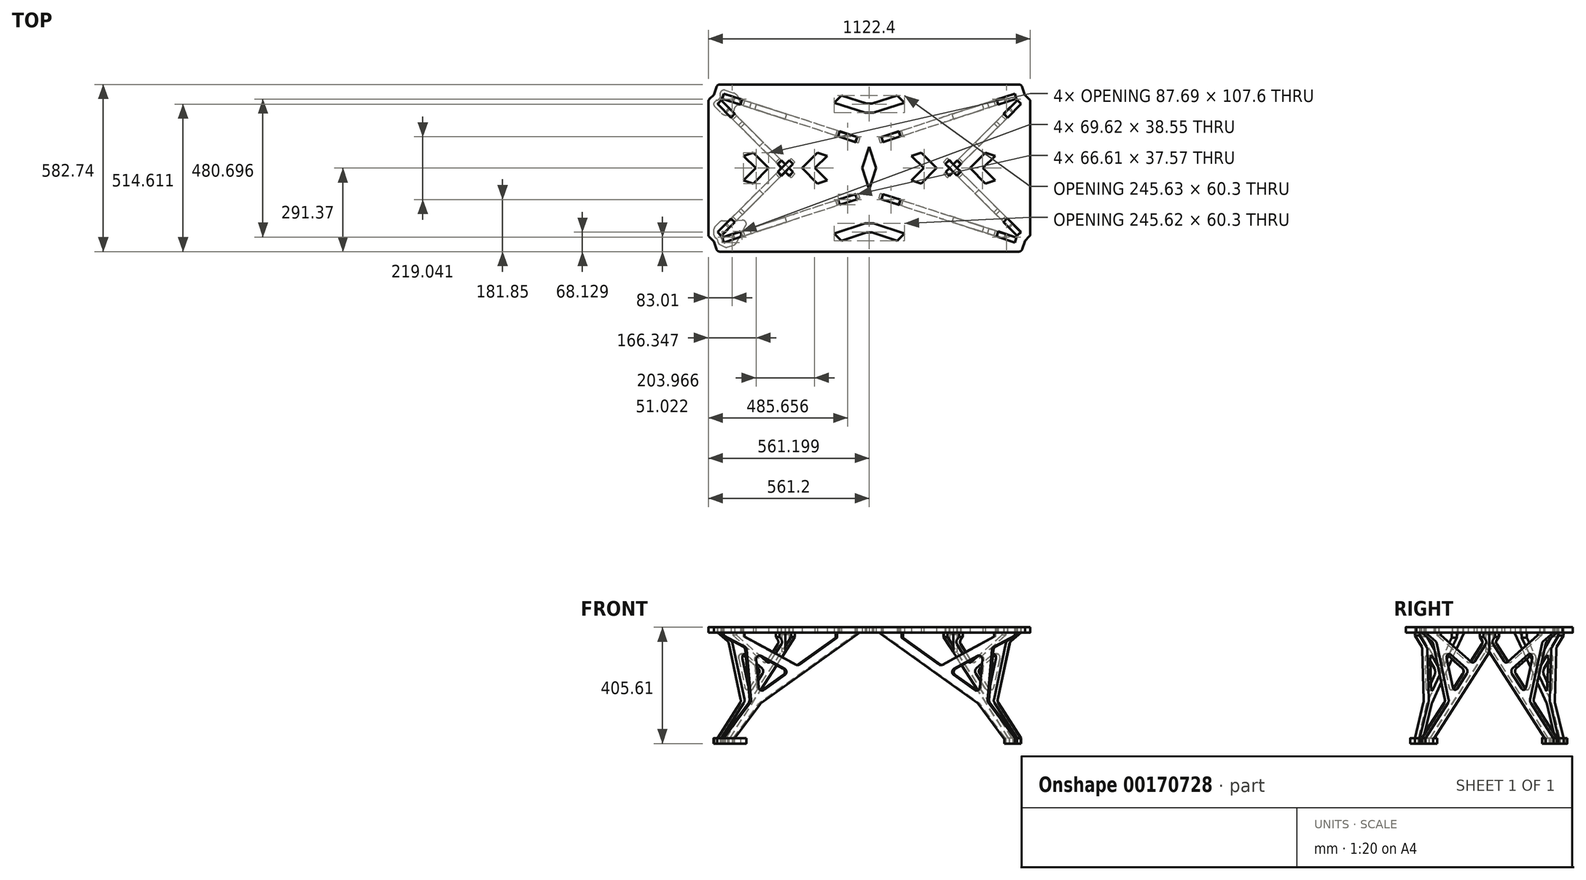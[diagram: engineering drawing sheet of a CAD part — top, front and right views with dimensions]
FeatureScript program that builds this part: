
annotation { "Feature Type Name" : "Feature", "Feature Type Description" : "" }
export const myFeature = defineFeature(function(context is Context, id is Id, definition is map)
    precondition{}
    {
        {
            var Q0;
            Q0=qCreatedBy(makeId("Top.planeOp"),FACE);
            var sketch = newSketch(context, id + "F0", { "sketchPlane" : qUnion([Q0])});
            skLineSegment(sketch, "E0.bottom", {"start": v(0, 0) * mm, "end": v(1117.6, 0) * mm});
            skLineSegment(sketch, "E0.top", {"start": v(0, 558.8) * mm, "end": v(1117.6, 558.8) * mm});
            skLineSegment(sketch, "E0.left", {"start": v(0, 0) * mm, "end": v(0, 558.8) * mm});
            skLineSegment(sketch, "E0.right", {"start": v(1117.6, 0) * mm, "end": v(1117.6, 558.8) * mm});
            skPoint(sketch, "E1", {"position": v(0, 279.4) * mm});
            skPoint(sketch, "E2", {"position": v(558.8, 558.8) * mm});
            skLineSegment(sketch, "E3", {"start": v(0, 279.4) * mm, "end": v(1117.6, 279.4) * mm, "construction": true});
            skLineSegment(sketch, "E4", {"start": v(558.8, 558.8) * mm, "end": v(558.8, 0) * mm, "construction": true});
            skLineSegment(sketch, "E5", {"start": v(0, 0) * mm, "end": v(42.87, 42.87) * mm, "construction": true});
            skLineSegment(sketch, "E6", {"start": v(0, 558.8) * mm, "end": v(33.89, 524.91) * mm, "construction": true});
            skLineSegment(sketch, "E7", {"start": v(1117.6, 558.8) * mm, "end": v(838.2, 279.4) * mm});
            skLineSegment(sketch, "E8", {"start": v(1117.6, 0) * mm, "end": v(838.2, 279.4) * mm});
            skLineSegment(sketch, "E9", {"start": v(279.4, 279.4) * mm, "end": v(299.6, 299.6) * mm});
            skLineSegment(sketch, "E10", {"start": v(279.4, 279.4) * mm, "end": v(299.6, 259.2) * mm});
            skLineSegment(sketch, "E11.0", {"start": v(19.05, 539.75) * mm, "end": v(1098.55, 539.75) * mm, "construction": true});
            skLineSegment(sketch, "E11.1", {"start": v(19.05, 19.05) * mm, "end": v(19.05, 32.52) * mm, "construction": true});
            skLineSegment(sketch, "E11.2", {"start": v(19.05, 19.05) * mm, "end": v(1098.55, 19.05) * mm, "construction": true});
            skLineSegment(sketch, "E11.3", {"start": v(1098.55, 19.05) * mm, "end": v(1098.55, 539.75) * mm, "construction": true});
            skLineSegment(sketch, "E12.trimOffspring", {"start": v(36.13, 49.6) * mm, "end": v(292.87, 306.34) * mm, "construction": true});
            skLineSegment(sketch, "E13", {"start": v(19.05, 539.75) * mm, "end": v(36.83, 533.97) * mm});
            skLineSegment(sketch, "E14", {"start": v(1098.55, 539.75) * mm, "end": v(558.8, 364.37) * mm});
            skLineSegment(sketch, "E15", {"start": v(1098.55, 19.05) * mm, "end": v(558.8, 194.43) * mm});
            skLineSegment(sketch, "E16", {"start": v(19.05, 19.05) * mm, "end": v(558.8, 194.43) * mm, "construction": true});
            skCircle(sketch, "E17", {"center": v(558.8, 279.4) * mm, "radius": 203.2 * mm});
            skPoint(sketch, "E18", {"position": v(330.81, 120.35) * mm});
            skPoint(sketch, "E19", {"position": v(442.7, 156.7) * mm});
            skPoint(sketch, "E20", {"position": v(406.46, 144.93) * mm});
            skPoint(sketch, "E21", {"position": v(406.46, 413.87) * mm});
            skPoint(sketch, "E22", {"position": v(370.23, 425.65) * mm});
            skPoint(sketch, "E23", {"position": v(711.14, 413.87) * mm});
            skPoint(sketch, "E24", {"position": v(747.37, 425.65) * mm});
            skPoint(sketch, "E25", {"position": v(674.9, 402.1) * mm});
            skPoint(sketch, "E26", {"position": v(711.14, 144.93) * mm});
            skPoint(sketch, "E27", {"position": v(674.9, 156.7) * mm});
            skPoint(sketch, "E28", {"position": v(747.37, 133.15) * mm});
            skLineSegment(sketch, "E29.bottom", {"start": v(-182.02, 259.46) * mm, "end": v(-105.82, 259.46) * mm});
            skLineSegment(sketch, "E29.top", {"start": v(-182.02, 278.51) * mm, "end": v(-105.82, 278.51) * mm});
            skLineSegment(sketch, "E29.left", {"start": v(-182.02, 259.46) * mm, "end": v(-182.02, 278.51) * mm});
            skLineSegment(sketch, "E29.right", {"start": v(-105.82, 259.46) * mm, "end": v(-105.82, 278.51) * mm});
            skLineSegment(sketch, "E30.bottom", {"start": v(-184.27, 473.53) * mm, "end": v(-82.67, 473.53) * mm});
            skLineSegment(sketch, "E30.top", {"start": v(-184.27, 492.58) * mm, "end": v(-82.67, 492.58) * mm});
            skLineSegment(sketch, "E30.left", {"start": v(-184.27, 473.53) * mm, "end": v(-184.27, 492.58) * mm});
            skLineSegment(sketch, "E30.right", {"start": v(-82.67, 473.53) * mm, "end": v(-82.67, 492.58) * mm});
            skPoint(sketch, "E31", {"position": v(-133.34, 483.2) * mm});
            skPoint(sketch, "E32", {"position": v(-133.34, 534) * mm});
            skLineSegment(sketch, "E33", {"start": v(-133.34, 534) * mm, "end": v(-123.82, 534) * mm});
            skLineSegment(sketch, "E34", {"start": v(-133.34, 534) * mm, "end": v(-142.87, 534) * mm});
            skLineSegment(sketch, "E35", {"start": v(-142.87, 534) * mm, "end": v(-144.35, 432.4) * mm});
            skLineSegment(sketch, "E36", {"start": v(-144.35, 432.4) * mm, "end": v(-125.29, 432.13) * mm});
            skLineSegment(sketch, "E37", {"start": v(-125.29, 432.13) * mm, "end": v(-123.82, 534) * mm});
            skPoint(sketch, "E38", {"position": v(-143.92, 268.99) * mm});
            skLineSegment(sketch, "E39", {"start": v(-153.47, 230.9) * mm, "end": v(-134.4, 230.9) * mm});
            skLineSegment(sketch, "E40", {"start": v(-134.4, 230.9) * mm, "end": v(-134.4, 307.1) * mm});
            skLineSegment(sketch, "E41", {"start": v(-134.4, 307.1) * mm, "end": v(-153.47, 307.1) * mm});
            skLineSegment(sketch, "E42", {"start": v(-153.47, 307.1) * mm, "end": v(-153.47, 230.9) * mm});
            skLineSegment(sketch, "E43.0", {"start": v(51.85, 19.7) * mm, "end": v(88.1, 31.47) * mm});
            skLineSegment(sketch, "E44.0", {"start": v(19.05, 29.07) * mm, "end": v(64.77, 43.92) * mm, "construction": true});
            skPoint(sketch, "E45", {"position": v(33.89, 33.89) * mm});
            skPoint(sketch, "E46", {"position": v(42.87, 42.87) * mm});
            skPoint(sketch, "E47", {"position": v(45.96, 37.81) * mm});
            skLineSegment(sketch, "E48", {"start": v(45.96, 37.81) * mm, "end": v(52.06, 19.05) * mm});
            skLineSegment(sketch, "E49", {"start": v(42.87, 42.87) * mm, "end": v(29.4, 56.33) * mm});
            skLineSegment(sketch, "E50.trimOffspring", {"start": v(19.05, 32.52) * mm, "end": v(19.05, 539.75) * mm, "construction": true});
            skLineSegment(sketch, "E51", {"start": v(29.4, 56.33) * mm, "end": v(56.34, 83.27) * mm});
            skLineSegment(sketch, "E52", {"start": v(69.8, 69.8) * mm, "end": v(42.87, 42.87) * mm});
            skLineSegment(sketch, "E53", {"start": v(45.96, 37.81) * mm, "end": v(82.2, 49.59) * mm});
            skPoint(sketch, "E54.visualSharp", {"position": v(19.05, 54.96) * mm});
            skPoint(sketch, "E55.orphan", {"position": v(53.81, 13.65) * mm});
            skPoint(sketch, "E56.visualSharp", {"position": v(69.8, 69.8) * mm});
            skPoint(sketch, "E57.visualSharp", {"position": v(82.2, 49.59) * mm});
            skLineSegment(sketch, "E58", {"start": v(245.72, 245.72) * mm, "end": v(232.25, 259.2) * mm});
            skLineSegment(sketch, "E59", {"start": v(299.6, 299.6) * mm, "end": v(286.14, 313.08) * mm});
            skLineSegment(sketch, "E60", {"start": v(265.93, 292.87) * mm, "end": v(286.14, 313.08) * mm});
            skLineSegment(sketch, "E61", {"start": v(299.6, 259.2) * mm, "end": v(286.14, 245.72) * mm});
            skPoint(sketch, "E62", {"position": v(245.72, 313.08) * mm});
            skLineSegment(sketch, "E63", {"start": v(245.72, 313.08) * mm, "end": v(232.25, 299.6) * mm});
            skPoint(sketch, "E64.orphan", {"position": v(272.66, 286.14) * mm});
            skLineSegment(sketch, "E65", {"start": v(36.13, 49.6) * mm, "end": v(90, 103.48) * mm});
            skPoint(sketch, "E66", {"position": v(403.28, 143.9) * mm});
            skLineSegment(sketch, "E67.0", {"start": v(19.05, 529.73) * mm, "end": v(33.89, 524.91) * mm, "construction": true});
            skLineSegment(sketch, "E68.0", {"start": v(51.85, 539.1) * mm, "end": v(88.09, 527.33) * mm, "construction": true});
            skPoint(sketch, "E69", {"position": v(33.89, 524.91) * mm});
            skPoint(sketch, "E70", {"position": v(45.96, 520.99) * mm});
            skPoint(sketch, "E71", {"position": v(42.87, 515.93) * mm});
            skLineSegment(sketch, "E72", {"start": v(42.87, 515.93) * mm, "end": v(29.4, 502.46) * mm, "construction": true});
            skLineSegment(sketch, "E73", {"start": v(45.96, 520.99) * mm, "end": v(51.85, 539.1) * mm});
            skLineSegment(sketch, "E74", {"start": v(51.85, 539.1) * mm, "end": v(82.05, 529.3) * mm});
            skLineSegment(sketch, "E75", {"start": v(76.16, 511.18) * mm, "end": v(45.96, 520.99) * mm});
            skLineSegment(sketch, "E76", {"start": v(33.89, 524.91) * mm, "end": v(24.9, 515.93) * mm});
            skLineSegment(sketch, "E77", {"start": v(33.89, 524.91) * mm, "end": v(37.81, 537) * mm});
            skLineSegment(sketch, "E78.0", {"start": v(43.7, 555.11) * mm, "end": v(55.78, 551.19) * mm});
            skLineSegment(sketch, "E79.0", {"start": v(11.43, 502.46) * mm, "end": v(20.42, 493.48) * mm});
            skPoint(sketch, "E80", {"position": v(122.52, 529.5) * mm});
            skLineSegment(sketch, "E81.trimOffspring", {"start": v(19.05, 526.28) * mm, "end": v(27.15, 518.18) * mm, "construction": true});
            skLineSegment(sketch, "E82.trimOffspring", {"start": v(19.05, 512.8) * mm, "end": v(29.4, 502.46) * mm, "construction": true});
            skPoint(sketch, "E83", {"position": v(20.42, 493.48) * mm});
            skPoint(sketch, "E84", {"position": v(20.42, 511.44) * mm});
            skArc(sketch, "E85.trimOffspring", {"start": v(20.42, 511.44) * mm, "mid": v(16.32, 502.46) * mm, "end": v(20.42, 493.48) * mm});
            skPoint(sketch, "E86", {"position": v(24.9, 515.93) * mm});
            skPoint(sketch, "E87", {"position": v(37.81, 537) * mm});
            skLineSegment(sketch, "E88.trimOffspring", {"start": v(45.96, 520.99) * mm, "end": v(82.2, 509.22) * mm, "construction": true});
            skLineSegment(sketch, "E89.trimOffspring", {"start": v(36.13, 509.2) * mm, "end": v(58.58, 486.75) * mm, "construction": true});
            skLineSegment(sketch, "E90.trimOffspring", {"start": v(48.9, 530.05) * mm, "end": v(79.1, 520.24) * mm});
            skArc(sketch, "E91", {"start": v(27.07, 515.93) * mm, "mid": v(37.83, 522.5) * mm, "end": v(38.8, 535.07) * mm});
            skPoint(sketch, "E91.third.point", {"position": v(12.19, 529.33) * mm});
            skPoint(sketch, "E92", {"position": v(39.77, 543.03) * mm});
            skPoint(sketch, "E93", {"position": v(55.78, 551.19) * mm});
            skLineSegment(sketch, "E94.trimOffspring", {"start": v(39.77, 543.03) * mm, "end": v(43.7, 555.11) * mm});
            skArc(sketch, "E95.trimOffspring", {"start": v(55.78, 551.19) * mm, "mid": v(46.26, 550.07) * mm, "end": v(39.77, 543.03) * mm});
            skLineSegment(sketch, "E96", {"start": v(33.89, 524.91) * mm, "end": v(176.88, 437.29) * mm, "construction": true});
            skPoint(sketch, "E97", {"position": v(51.85, 462.05) * mm});
            skPoint(sketch, "E98", {"position": v(98.05, 537.45) * mm});
            skLineSegment(sketch, "E99", {"start": v(64.47, 463.46) * mm, "end": v(82.68, 465.5) * mm});
            skLineSegment(sketch, "E100", {"start": v(108.97, 508.42) * mm, "end": v(102.52, 525.56) * mm});
            skPoint(sketch, "E101", {"position": v(64.47, 463.46) * mm});
            skPoint(sketch, "E102", {"position": v(102.52, 525.56) * mm});
            skArc(sketch, "E103", {"start": v(42.87, 471.03) * mm, "mid": v(54.55, 464.49) * mm, "end": v(67.94, 463.92) * mm});
            skArc(sketch, "E104", {"start": v(103.55, 522.31) * mm, "mid": v(97.05, 534.27) * mm, "end": v(85.53, 541.52) * mm});
            skArc(sketch, "E105", {"start": v(104, 499.9) * mm, "mid": v(89.94, 490.56) * mm, "end": v(88, 473.8) * mm});
            skPoint(sketch, "E105.first.point", {"position": v(92.23, 466.57) * mm});
            skPoint(sketch, "E105.second.point", {"position": v(112.36, 499.42) * mm});
            skLineSegment(sketch, "E106.trimOffspring", {"start": v(93.52, 465.28) * mm, "end": v(279.4, 279.4) * mm, "construction": true});
            skLineSegment(sketch, "E107.trimOffspring", {"start": v(114.1, 498.85) * mm, "end": v(552.91, 356.27) * mm, "construction": true});
            skArc(sketch, "E108.filletArc", {"start": v(82.68, 465.5) * mm, "mid": v(87.31, 468.38) * mm, "end": v(88, 473.8) * mm});
            skArc(sketch, "E109.filletArc", {"start": v(104, 499.9) * mm, "mid": v(108.5, 502.97) * mm, "end": v(108.97, 508.42) * mm});
            skLineSegment(sketch, "E110", {"start": v(38.62, 539.48) * mm, "end": v(39.77, 543.03) * mm});
            skLineSegment(sketch, "E111.trimOffspring", {"start": v(20.42, 511.44) * mm, "end": v(11.43, 502.46) * mm});
            skLineSegment(sketch, "E112", {"start": v(20.42, 511.44) * mm, "end": v(23.06, 514.09) * mm});
            skArc(sketch, "E113.filletArc", {"start": v(27.07, 515.93) * mm, "mid": v(24.9, 515.37) * mm, "end": v(23.06, 514.09) * mm});
            skArc(sketch, "E114.filletArc", {"start": v(38.62, 539.48) * mm, "mid": v(38.31, 537.26) * mm, "end": v(38.8, 535.07) * mm});
            skLineSegment(sketch, "E115.trimOffspring", {"start": v(42.87, 471.03) * mm, "end": v(65.33, 448.56) * mm});
            skLineSegment(sketch, "E116", {"start": v(42.87, 471.03) * mm, "end": v(20.42, 493.48) * mm});
            skLineSegment(sketch, "E117.trimOffspring", {"start": v(85.53, 541.52) * mm, "end": v(122.52, 529.5) * mm});
            skLineSegment(sketch, "E118", {"start": v(85.53, 541.52) * mm, "end": v(55.78, 551.19) * mm});
            skLineSegment(sketch, "E119.trimOffspring", {"start": v(108.06, 510.83) * mm, "end": v(558.8, 364.37) * mm});
            skLineSegment(sketch, "E120.trimOffspring", {"start": v(80.11, 465.22) * mm, "end": v(292.87, 252.46) * mm, "construction": true});
            skLineSegment(sketch, "E121.trimOffspring", {"start": v(51.86, 480) * mm, "end": v(286.14, 245.72) * mm, "construction": true});
            skLineSegment(sketch, "E122", {"start": v(29.4, 502.46) * mm, "end": v(51.85, 480.02) * mm, "construction": true});
            skLineSegment(sketch, "E123.0", {"start": v(42.87, 516.04) * mm, "end": v(29.29, 502.46) * mm});
            skLineSegment(sketch, "E124.0", {"start": v(29.29, 502.46) * mm, "end": v(56.32, 475.44) * mm});
            skLineSegment(sketch, "E125.trimOffspring", {"start": v(88.2, 470.6) * mm, "end": v(92.23, 466.57) * mm, "construction": true});
            skLineSegment(sketch, "E126", {"start": v(42.87, 515.93) * mm, "end": v(65.32, 493.48) * mm, "construction": true});
            skLineSegment(sketch, "E127", {"start": v(69.8, 489.03) * mm, "end": v(56.32, 475.54) * mm, "construction": true});
            skLineSegment(sketch, "E128", {"start": v(56.32, 475.54) * mm, "end": v(51.86, 480) * mm});
            skLineSegment(sketch, "E129.0", {"start": v(69.9, 489.01) * mm, "end": v(56.32, 475.44) * mm});
            skLineSegment(sketch, "E130", {"start": v(76.16, 511.18) * mm, "end": v(82.2, 509.22) * mm});
            skLineSegment(sketch, "E131", {"start": v(82.2, 509.22) * mm, "end": v(88.09, 527.33) * mm, "construction": true});
            skLineSegment(sketch, "E132", {"start": v(88.09, 527.33) * mm, "end": v(82.05, 529.3) * mm, "construction": true});
            skLineSegment(sketch, "E133.0", {"start": v(82.25, 509.12) * mm, "end": v(88.18, 527.38) * mm});
            skLineSegment(sketch, "E134", {"start": v(82.27, 509.2) * mm, "end": v(82.2, 509.22) * mm});
            skLineSegment(sketch, "E135", {"start": v(558.8, 374.39) * mm, "end": v(552.91, 356.27) * mm, "construction": true});
            skLineSegment(sketch, "E136", {"start": v(413.61, 421.56) * mm, "end": v(407.73, 403.45) * mm, "construction": true});
            skPoint(sketch, "E137", {"position": v(480.32, 379.86) * mm});
            skLineSegment(sketch, "E138", {"start": v(480.32, 379.86) * mm, "end": v(450.12, 389.67) * mm});
            skLineSegment(sketch, "E139", {"start": v(450.12, 389.67) * mm, "end": v(456, 407.79) * mm});
            skLineSegment(sketch, "E140", {"start": v(456, 407.79) * mm, "end": v(516.4, 388.17) * mm});
            skLineSegment(sketch, "E141", {"start": v(516.4, 388.17) * mm, "end": v(510.5, 370.05) * mm});
            skLineSegment(sketch, "E142", {"start": v(510.5, 370.05) * mm, "end": v(480.32, 379.86) * mm});
            skLineSegment(sketch, "E143", {"start": v(19.05, 19.05) * mm, "end": v(48.9, 28.75) * mm});
            skPoint(sketch, "E144", {"position": v(1068.7, 28.75) * mm});
            skLineSegment(sketch, "E145", {"start": v(1065.74, 19.68) * mm, "end": v(1071.63, 37.8) * mm});
            skLineSegment(sketch, "E146", {"start": v(1071.63, 37.8) * mm, "end": v(1035.4, 49.58) * mm});
            skLineSegment(sketch, "E147", {"start": v(1035.4, 49.58) * mm, "end": v(1029.51, 31.45) * mm});
            skPoint(sketch, "E148", {"position": v(1073.92, 43.68) * mm});
            skLineSegment(sketch, "E149", {"start": v(1073.92, 43.68) * mm, "end": v(1087.39, 57.15) * mm});
            skLineSegment(sketch, "E150", {"start": v(1087.39, 57.15) * mm, "end": v(1060.45, 84.1) * mm});
            skLineSegment(sketch, "E151", {"start": v(1060.45, 84.1) * mm, "end": v(1046.98, 70.62) * mm});
            skLineSegment(sketch, "E152", {"start": v(1046.98, 70.62) * mm, "end": v(1073.92, 43.68) * mm});
            skPoint(sketch, "E153", {"position": v(1053.71, 77.36) * mm});
            skLineSegment(sketch, "E154", {"start": v(1053.71, 77.36) * mm, "end": v(1080.65, 50.42) * mm, "construction": true});
            skPoint(sketch, "E155", {"position": v(1068.7, 530.05) * mm});
            skLineSegment(sketch, "E156", {"start": v(1071.63, 521) * mm, "end": v(1065.75, 539.1) * mm});
            skLineSegment(sketch, "E157", {"start": v(1065.75, 539.1) * mm, "end": v(1029.52, 527.33) * mm});
            skLineSegment(sketch, "E158", {"start": v(1029.52, 527.33) * mm, "end": v(1035.4, 509.22) * mm});
            skLineSegment(sketch, "E159", {"start": v(1035.4, 509.22) * mm, "end": v(1071.63, 521) * mm});
            skPoint(sketch, "E160", {"position": v(1074.74, 515.94) * mm});
            skLineSegment(sketch, "E161", {"start": v(1074.74, 515.94) * mm, "end": v(1088.2, 502.47) * mm});
            skLineSegment(sketch, "E162", {"start": v(1088.2, 502.47) * mm, "end": v(1061.26, 475.53) * mm});
            skLineSegment(sketch, "E163", {"start": v(1061.26, 475.53) * mm, "end": v(1047.8, 489) * mm});
            skLineSegment(sketch, "E164", {"start": v(1047.8, 489) * mm, "end": v(1074.74, 515.94) * mm});
            skPoint(sketch, "E165", {"position": v(1054.53, 482.26) * mm});
            skLineSegment(sketch, "E166", {"start": v(1054.53, 482.26) * mm, "end": v(1081.47, 509.2) * mm, "construction": true});
            skLineSegment(sketch, "E167", {"start": v(82.2, 49.59) * mm, "end": v(88.1, 31.47) * mm});
            skLineSegment(sketch, "E168.trimOffspring", {"start": v(88.1, 31.47) * mm, "end": v(561.74, 185.37) * mm, "construction": true});
            skLineSegment(sketch, "E169.trimOffspring", {"start": v(82.2, 49.59) * mm, "end": v(555.86, 203.48) * mm, "construction": true});
            skLineSegment(sketch, "E170.trimOffspring", {"start": v(69.8, 69.8) * mm, "end": v(279.4, 279.4) * mm, "construction": true});
            skLineSegment(sketch, "E171", {"start": v(69.8, 69.8) * mm, "end": v(56.34, 83.28) * mm});
            skLineSegment(sketch, "E172", {"start": v(1065.74, 19.68) * mm, "end": v(1029.51, 31.45) * mm});
            skPoint(sketch, "E173.end.orphan", {"position": v(1083.72, 524.92) * mm});
            skLineSegment(sketch, "E174.0", {"start": v(42.87, 516.04) * mm, "end": v(69.9, 489.01) * mm});
            skLineSegment(sketch, "E175.trimOffspring", {"start": v(106.94, 501.18) * mm, "end": v(112.36, 499.42) * mm, "construction": true});
            skLineSegment(sketch, "E176.trimOffspring", {"start": v(103.55, 522.31) * mm, "end": v(561.74, 373.43) * mm, "construction": true});
            skLineSegment(sketch, "E177.0", {"start": v(51.8, 539.2) * mm, "end": v(88.18, 527.38) * mm});
            skLineSegment(sketch, "E177.1", {"start": v(45.87, 520.94) * mm, "end": v(51.8, 539.2) * mm});
            skLineSegment(sketch, "E177.2", {"start": v(45.87, 520.94) * mm, "end": v(82.25, 509.12) * mm});
            skSolve(sketch);
        }
        {
            var Q0;
            Q0=sQuery(id+"F0.wireOp",EDGE,"E16");
            cPlane(context, id + "F1", {"entities" : qUnion([Q0]), "cplaneType" : CPlaneType.LINE_ANGLE, "offset" : 25.4 * mm, "angle" : 0 * degree, "width" : 152.4 * mm, "height" : 152.4 * mm});
        }
        {
            var Q0;
            Q0=qCreatedBy(id+"F1.planeOp",FACE);
            var sketch = newSketch(context, id + "F2", { "sketchPlane" : qUnion([Q0])});
            skLineSegment(sketch, "E178.MirrorCS", {"start": v(-55.4, 387.35) * mm, "end": v(-55.4, 405.61) * mm});
            skLineSegment(sketch, "E179.MirrorCS", {"start": v(-55.4, 19.05) * mm, "end": v(-55.4, 0) * mm});
            skLineSegment(sketch, "E180.MirrorCS", {"start": v(-55.4, 0) * mm, "end": v(-93.5, 0) * mm});
            skLineSegment(sketch, "E181.MirrorCS", {"start": v(-131.6, 387.35) * mm, "end": v(-122.07, 387.35) * mm});
            skLineSegment(sketch, "E182.MirrorCS", {"start": v(-122.07, 405.61) * mm, "end": v(-122.07, 387.35) * mm});
            skLineSegment(sketch, "E183.MirrorCS", {"start": v(-93.5, 0) * mm, "end": v(-93.5, 19.05) * mm});
            skLineSegment(sketch, "E184.MirrorCS", {"start": v(-131.6, 387.35) * mm, "end": v(-131.6, 373.26) * mm});
            skPoint(sketch, "E185.MirrorP", {"position": v(-87.16, 0) * mm});
            skLineSegment(sketch, "E186.MirrorCS", {"start": v(-199.46, 139.13) * mm, "end": v(-199.94, 139.68) * mm});
            skLineSegment(sketch, "E187.MirrorCS", {"start": v(-131.6, 373.26) * mm, "end": v(-319.77, 274.75) * mm});
            skPoint(sketch, "E188.MirrorP", {"position": v(-55.4, 19.05) * mm});
            skLineSegment(sketch, "E189.MirrorCS", {"start": v(-189.04, 192.2) * mm, "end": v(-187.9, 197.99) * mm});
            skLineSegment(sketch, "E190.MirrorCS", {"start": v(-199.46, 139.13) * mm, "end": v(-199.43, 139.3) * mm});
            skLineSegment(sketch, "E191.trimOffspring", {"start": v(-199.94, 139.68) * mm, "end": v(-199.43, 139.3) * mm});
            skLineSegment(sketch, "E192", {"start": v(-480.35, 387.35) * mm, "end": v(-470.81, 387.35) * mm});
            skLineSegment(sketch, "E193", {"start": v(-543.85, 387.35) * mm, "end": v(-553.36, 387.35) * mm});
            skLineSegment(sketch, "E194", {"start": v(-470.81, 387.35) * mm, "end": v(-470.81, 369.53) * mm});
            skLineSegment(sketch, "E195", {"start": v(-543.85, 387.35) * mm, "end": v(-543.85, 405.61) * mm});
            skLineSegment(sketch, "E196", {"start": v(-480.35, 387.35) * mm, "end": v(-480.35, 405.61) * mm});
            skLineSegment(sketch, "E197", {"start": v(-553.36, 387.35) * mm, "end": v(-192.29, 141.35) * mm});
            skLineSegment(sketch, "E198.trimOffspring", {"start": v(-470.81, 369.53) * mm, "end": v(-332.8, 275.5) * mm});
            skPoint(sketch, "E199", {"position": v(-320.5, 267.12) * mm});
            skLineSegment(sketch, "E200", {"start": v(-55.4, 19.05) * mm, "end": v(-152.69, 143.25) * mm});
            skLineSegment(sketch, "E201.0", {"start": v(-80.4, -0.53) * mm, "end": v(-80.8, 0) * mm});
            skLineSegment(sketch, "E202", {"start": v(-93.5, 19.05) * mm, "end": v(-95.73, 19.05) * mm});
            skLineSegment(sketch, "E203.trimOffspring", {"start": v(-95.73, 19.05) * mm, "end": v(-189.44, 138.69) * mm});
            skLineSegment(sketch, "E204.0", {"start": v(-55.4, 377.31) * mm, "end": v(-132.58, 336.91) * mm});
            skLineSegment(sketch, "E205.trimOffspring", {"start": v(-279.27, 239.03) * mm, "end": v(-202.97, 187.05) * mm});
            skLineSegment(sketch, "E206", {"start": v(-55.4, 377.31) * mm, "end": v(-55.4, 387.35) * mm});
            skLineSegment(sketch, "E207", {"start": v(-155.34, 152.24) * mm, "end": v(-139.33, 326.82) * mm});
            skLineSegment(sketch, "E208.0", {"start": v(-183.17, 196.38) * mm, "end": v(-174.32, 292.94) * mm});
            skLineSegment(sketch, "E209.trimOffspring", {"start": v(-192.86, 305.35) * mm, "end": v(-278, 260.77) * mm});
            skPoint(sketch, "E210.trimOffspring.end.orphan", {"position": v(-160.66, 158.22) * mm});
            skPoint(sketch, "E211.orphan", {"position": v(-334.34, 267.12) * mm});
            skPoint(sketch, "E212.visualSharp", {"position": v(-296.77, 250.95) * mm});
            skArc(sketch, "E212.filletArc", {"start": v(-278, 260.77) * mm, "mid": v(-284.8, 250.26) * mm, "end": v(-279.27, 239.03) * mm});
            skPoint(sketch, "E213.visualSharp", {"position": v(-172.2, 316.17) * mm});
            skArc(sketch, "E213.filletArc", {"start": v(-174.32, 292.94) * mm, "mid": v(-179.9, 304.65) * mm, "end": v(-192.86, 305.35) * mm});
            skPoint(sketch, "E214.visualSharp", {"position": v(-185.14, 174.9) * mm});
            skArc(sketch, "E214.filletArc", {"start": v(-202.97, 187.05) * mm, "mid": v(-190.4, 186.05) * mm, "end": v(-183.17, 196.38) * mm});
            skPoint(sketch, "E215.visualSharp", {"position": v(-190.66, 140.24) * mm});
            skArc(sketch, "E215.filletArc", {"start": v(-189.44, 138.69) * mm, "mid": v(-190.76, 140.13) * mm, "end": v(-192.29, 141.35) * mm});
            skPoint(sketch, "E216.visualSharp", {"position": v(-326.52, 271.22) * mm});
            skArc(sketch, "E216.filletArc", {"start": v(-332.8, 275.5) * mm, "mid": v(-326.4, 273.32) * mm, "end": v(-319.77, 274.75) * mm});
            skPoint(sketch, "E217.visualSharp", {"position": v(-138.7, 333.7) * mm});
            skArc(sketch, "E217.filletArc", {"start": v(-132.58, 336.91) * mm, "mid": v(-137.24, 332.72) * mm, "end": v(-139.33, 326.82) * mm});
            skPoint(sketch, "E218.visualSharp", {"position": v(-155.8, 147.22) * mm});
            skArc(sketch, "E218.filletArc", {"start": v(-155.34, 152.24) * mm, "mid": v(-154.87, 147.5) * mm, "end": v(-152.69, 143.25) * mm});
            skLineSegment(sketch, "E219", {"start": v(-480.35, 405.61) * mm, "end": v(-543.85, 405.61) * mm});
            skLineSegment(sketch, "E220", {"start": v(-122.07, 405.61) * mm, "end": v(-55.4, 405.61) * mm});
            skSolve(sketch);
        }
        {
            var Q0;
            Q0=makeQuery(id+"F2.imprint","IMPRINT",FACE,{"disambiguationData":[TD([[makeQuery(id+"F2.imprint","IMPRINT",EDGE,{"derivedFrom":sQuery(id+"F2.wireOp",EDGE,"E187.MirrorCS")}),1.0]])]});
            extrude(context, id + "F3", {"entities" : qUnion([Q0]), "endBound" : BoundingType.SYMMETRIC, "depth" : 18.26 * mm});
        }
        {
            var Q0;
            Q0=sQuery(id+"F0.wireOp",EDGE,"E12.trimOffspring");
            cPlane(context, id + "F4", {"entities" : qUnion([Q0]), "cplaneType" : CPlaneType.LINE_ANGLE, "offset" : 25.4 * mm, "angle" : 90 * degree, "width" : 152.4 * mm, "height" : 152.4 * mm});
        }
        {
            var Q0;
            Q0=qCreatedBy(id+"F4.planeOp",FACE);
            var sketch = newSketch(context, id + "F5", { "sketchPlane" : qUnion([Q0])});
            skLineSegment(sketch, "E221.MirrorCS", {"start": v(347.5, 387.35) * mm, "end": v(357.03, 387.35) * mm});
            skArc(sketch, "E222.MirrorCS", {"start": v(110.82, 356.2) * mm, "mid": v(114.2, 353.14) * mm, "end": v(116.29, 349.08) * mm});
            skArc(sketch, "E223.MirrorCS", {"start": v(174.96, 154.1) * mm, "mid": v(175.2, 147.64) * mm, "end": v(172.2, 141.9) * mm});
            skLineSegment(sketch, "E224.MirrorCS", {"start": v(347.5, 371.58) * mm, "end": v(356.35, 363.54) * mm});
            skLineSegment(sketch, "E225.MirrorCS", {"start": v(60.62, 19.05) * mm, "end": v(60.62, 0) * mm});
            skLineSegment(sketch, "E226.MirrorCS", {"start": v(423.7, 387.35) * mm, "end": v(414.18, 387.35) * mm});
            skLineSegment(sketch, "E227.MirrorCS", {"start": v(347.5, 371.58) * mm, "end": v(347.5, 387.35) * mm});
            skLineSegment(sketch, "E228.MirrorCS", {"start": v(60.62, 387.35) * mm, "end": v(60.62, 405.61) * mm});
            skArc(sketch, "E229.MirrorCS", {"start": v(303.4, 286.35) * mm, "mid": v(295.76, 282.3) * mm, "end": v(287.3, 284.1) * mm});
            skArc(sketch, "E230.MirrorCS", {"start": v(217.03, 191.26) * mm, "mid": v(204.83, 187.41) * mm, "end": v(195.47, 196.14) * mm});
            skLineSegment(sketch, "E231.MirrorCS", {"start": v(357.03, 387.35) * mm, "end": v(357.03, 405.61) * mm});
            skLineSegment(sketch, "E232.MirrorCS", {"start": v(414.18, 387.35) * mm, "end": v(414.18, 405.61) * mm});
            skArc(sketch, "E233.MirrorCS", {"start": v(356.35, 363.54) * mm, "mid": v(360.5, 354.75) * mm, "end": v(357.22, 345.6) * mm});
            skArc(sketch, "E234.MirrorCS", {"start": v(261.62, 262.66) * mm, "mid": v(267.5, 253.63) * mm, "end": v(264.33, 243.33) * mm});
            skLineSegment(sketch, "E235.MirrorCS", {"start": v(136.81, 387.35) * mm, "end": v(136.81, 377.45) * mm});
            skLineSegment(sketch, "E236.MirrorCS", {"start": v(136.81, 387.35) * mm, "end": v(127.29, 387.35) * mm});
            skLineSegment(sketch, "E237.MirrorCS", {"start": v(98.72, 0) * mm, "end": v(98.72, 19.05) * mm});
            skLineSegment(sketch, "E238.MirrorCS", {"start": v(103.51, 19.05) * mm, "end": v(98.72, 19.05) * mm});
            skLineSegment(sketch, "E239.MirrorCS", {"start": v(127.29, 405.61) * mm, "end": v(127.29, 387.35) * mm});
            skArc(sketch, "E240.MirrorCS", {"start": v(165.35, 296.24) * mm, "mid": v(169.78, 309.98) * mm, "end": v(184.2, 310.69) * mm});
            skPoint(sketch, "E241.MirrorP", {"position": v(274.58, 254.62) * mm});
            skPoint(sketch, "E242.MirrorP", {"position": v(177.04, 147.22) * mm});
            skPoint(sketch, "E243.MirrorP", {"position": v(365.75, 355) * mm});
            skPoint(sketch, "E244.MirrorP", {"position": v(114.9, 353.68) * mm});
            skPoint(sketch, "E245.MirrorP", {"position": v(92.38, 0) * mm});
            skPoint(sketch, "E246.MirrorP", {"position": v(60.62, 19.05) * mm});
            skLineSegment(sketch, "E247.MirrorCS", {"start": v(60.62, 19.05) * mm, "end": v(172.2, 141.9) * mm});
            skLineSegment(sketch, "E248.MirrorCS", {"start": v(116.29, 349.08) * mm, "end": v(174.96, 154.1) * mm});
            skLineSegment(sketch, "E249.MirrorCS", {"start": v(184.2, 310.69) * mm, "end": v(261.62, 262.66) * mm});
            skLineSegment(sketch, "E250.MirrorCS", {"start": v(103.51, 19.05) * mm, "end": v(376.24, 319.33) * mm});
            skPoint(sketch, "E251.MirrorP", {"position": v(296.29, 278.52) * mm});
            skPoint(sketch, "E252.MirrorP", {"position": v(155.67, 328.39) * mm});
            skLineSegment(sketch, "E253.MirrorCS", {"start": v(303.4, 286.35) * mm, "end": v(357.22, 345.6) * mm});
            skLineSegment(sketch, "E254.MirrorCS", {"start": v(60.62, 0) * mm, "end": v(98.72, 0) * mm});
            skLineSegment(sketch, "E255.MirrorCS", {"start": v(136.81, 377.45) * mm, "end": v(287.3, 284.1) * mm});
            skLineSegment(sketch, "E256.MirrorCS", {"start": v(165.35, 296.24) * mm, "end": v(195.47, 196.14) * mm});
            skLineSegment(sketch, "E257.MirrorCS", {"start": v(217.03, 191.26) * mm, "end": v(264.33, 243.33) * mm});
            skLineSegment(sketch, "E258.MirrorCS", {"start": v(60.62, 387.35) * mm, "end": v(110.82, 356.2) * mm});
            skPoint(sketch, "E259.MirrorP", {"position": v(201.94, 174.64) * mm});
            skLineSegment(sketch, "E260.MirrorCS", {"start": v(423.7, 371.58) * mm, "end": v(423.7, 387.35) * mm});
            skLineSegment(sketch, "E261.trimOffspring", {"start": v(394.96, 339.94) * mm, "end": v(423.7, 371.58) * mm});
            skLineSegment(sketch, "E262.0", {"start": v(376.24, 380.97) * mm, "end": v(376.24, 319.33) * mm});
            skLineSegment(sketch, "E263.0", {"start": v(394.96, 380.97) * mm, "end": v(394.96, 339.94) * mm});
            skLineSegment(sketch, "E264.trimOffspring", {"start": v(376.24, 380.97) * mm, "end": v(394.96, 380.97) * mm});
            skLineSegment(sketch, "E265", {"start": v(414.18, 405.61) * mm, "end": v(357.03, 405.61) * mm});
            skLineSegment(sketch, "E266.trimOffspring", {"start": v(127.29, 405.61) * mm, "end": v(60.62, 405.61) * mm});
            skSolve(sketch);
        }
        {
            var Q0;
            Q0 = qSketchRegion(id + "F5", true);
            extrude(context, id + "F6", {"entities" : qUnion([Q0]), "endBound" : BoundingType.SYMMETRIC, "depth" : 18.26 * mm});
        }
        {
            var Q0;
            Q0=sQuery(id+"F0.wireOp",EDGE,"E89.trimOffspring");
            cPlane(context, id + "F7", {"entities" : qUnion([Q0]), "cplaneType" : CPlaneType.LINE_ANGLE, "offset" : 25.4 * mm, "angle" : 90 * degree, "width" : 152.4 * mm, "height" : 152.4 * mm});
        }
        {
            var Q0;
            Q0=qCreatedBy(id+"F7.planeOp",FACE);
            var sketch = newSketch(context, id + "F8", { "sketchPlane" : qUnion([Q0])});
            skLineSegment(sketch, "E267.MirrorCS", {"start": v(-28.57, 387.35) * mm, "end": v(-19.05, 387.35) * mm});
            skLineSegment(sketch, "E268.MirrorCS", {"start": v(47.62, 387.35) * mm, "end": v(38.1, 387.35) * mm});
            skLineSegment(sketch, "E269.MirrorCS", {"start": v(258.31, 387.35) * mm, "end": v(267.84, 387.35) * mm});
            skLineSegment(sketch, "E270.MirrorCS", {"start": v(334.5, 387.35) * mm, "end": v(334.5, 405.61) * mm});
            skLineSegment(sketch, "E271.MirrorCS", {"start": v(334.5, 19.05) * mm, "end": v(334.5, 0) * mm});
            skLineSegment(sketch, "E272.MirrorCS", {"start": v(258.31, 387.35) * mm, "end": v(258.31, 377.45) * mm});
            skPoint(sketch, "E273.MirrorP", {"position": v(334.5, 19.05) * mm});
            skLineSegment(sketch, "E274.MirrorCS", {"start": v(296.4, 0) * mm, "end": v(296.4, 19.05) * mm});
            skLineSegment(sketch, "E275.MirrorCS", {"start": v(267.84, 405.61) * mm, "end": v(267.84, 387.35) * mm});
            skLineSegment(sketch, "E276.MirrorCS", {"start": v(91.73, 286.35) * mm, "end": v(37.91, 345.6) * mm});
            skLineSegment(sketch, "E277.MirrorCS", {"start": v(334.5, 0) * mm, "end": v(296.4, 0) * mm});
            skLineSegment(sketch, "E278.MirrorCS", {"start": v(178.1, 191.26) * mm, "end": v(130.8, 243.33) * mm});
            skLineSegment(sketch, "E279.MirrorCS", {"start": v(334.5, 19.05) * mm, "end": v(222.92, 141.9) * mm});
            skPoint(sketch, "E280.MirrorP", {"position": v(302.75, 0) * mm});
            skLineSegment(sketch, "E281.MirrorCS", {"start": v(-28.57, 371.58) * mm, "end": v(-28.57, 387.35) * mm});
            skLineSegment(sketch, "E282.MirrorCS", {"start": v(38.1, 387.35) * mm, "end": v(38.1, 405.61) * mm});
            skLineSegment(sketch, "E283.MirrorCS", {"start": v(334.5, 387.35) * mm, "end": v(284.3, 356.2) * mm});
            skLineSegment(sketch, "E284.MirrorCS", {"start": v(-19.05, 387.35) * mm, "end": v(-19.05, 405.61) * mm});
            skLineSegment(sketch, "E285.MirrorCS", {"start": v(210.92, 310.69) * mm, "end": v(133.5, 262.66) * mm});
            skLineSegment(sketch, "E286.0", {"start": v(18.88, 380.54) * mm, "end": v(0.17, 380.54) * mm});
            skLineSegment(sketch, "E287.0", {"start": v(291.61, 19.05) * mm, "end": v(-28.57, 371.58) * mm});
            skLineSegment(sketch, "E288", {"start": v(291.61, 19.05) * mm, "end": v(296.4, 19.05) * mm});
            skLineSegment(sketch, "E289.0", {"start": v(258.31, 377.45) * mm, "end": v(107.83, 284.1) * mm});
            skLineSegment(sketch, "E290", {"start": v(47.62, 371.58) * mm, "end": v(47.62, 387.35) * mm});
            skLineSegment(sketch, "E291", {"start": v(47.62, 371.58) * mm, "end": v(38.77, 363.54) * mm});
            skLineSegment(sketch, "E292", {"start": v(278.84, 349.08) * mm, "end": v(220.16, 154.1) * mm});
            skLineSegment(sketch, "E293.0", {"start": v(229.78, 296.24) * mm, "end": v(199.66, 196.14) * mm});
            skPoint(sketch, "E294.visualSharp", {"position": v(98.84, 278.52) * mm});
            skArc(sketch, "E294.filletArc", {"start": v(91.73, 286.35) * mm, "mid": v(99.37, 282.3) * mm, "end": v(107.83, 284.1) * mm});
            skPoint(sketch, "E295.visualSharp", {"position": v(239.46, 328.39) * mm});
            skArc(sketch, "E295.filletArc", {"start": v(229.78, 296.24) * mm, "mid": v(225.35, 309.98) * mm, "end": v(210.92, 310.69) * mm});
            skPoint(sketch, "E296.visualSharp", {"position": v(193.19, 174.64) * mm});
            skArc(sketch, "E296.filletArc", {"start": v(178.1, 191.26) * mm, "mid": v(190.3, 187.41) * mm, "end": v(199.66, 196.14) * mm});
            skPoint(sketch, "E297.visualSharp", {"position": v(120.55, 254.62) * mm});
            skArc(sketch, "E297.filletArc", {"start": v(133.5, 262.66) * mm, "mid": v(127.62, 253.63) * mm, "end": v(130.8, 243.33) * mm});
            skPoint(sketch, "E298.visualSharp", {"position": v(218.1, 147.22) * mm});
            skArc(sketch, "E298.filletArc", {"start": v(220.16, 154.1) * mm, "mid": v(219.94, 147.64) * mm, "end": v(222.92, 141.9) * mm});
            skPoint(sketch, "E299.visualSharp", {"position": v(29.37, 355) * mm});
            skArc(sketch, "E299.filletArc", {"start": v(38.77, 363.54) * mm, "mid": v(34.63, 354.75) * mm, "end": v(37.91, 345.6) * mm});
            skPoint(sketch, "E300.visualSharp", {"position": v(280.22, 353.68) * mm});
            skArc(sketch, "E300.filletArc", {"start": v(284.3, 356.2) * mm, "mid": v(280.92, 353.14) * mm, "end": v(278.84, 349.08) * mm});
            skLineSegment(sketch, "E301.0", {"start": v(18.88, 380.54) * mm, "end": v(18.88, 405.61) * mm});
            skLineSegment(sketch, "E302.0", {"start": v(0.17, 380.54) * mm, "end": v(0.17, 405.61) * mm});
            skLineSegment(sketch, "E303", {"start": v(334.5, 405.61) * mm, "end": v(267.84, 405.61) * mm});
            skPoint(sketch, "E304.start.orphan", {"position": v(263.08, 387.35) * mm});
            skLineSegment(sketch, "E305.trimOffspring", {"start": v(38.1, 405.61) * mm, "end": v(18.88, 405.61) * mm});
            skLineSegment(sketch, "E306.trimOffspring", {"start": v(0.17, 405.61) * mm, "end": v(-19.05, 405.61) * mm});
            skSolve(sketch);
        }
        {
            var Q0;
            Q0=makeQuery(id+"F8.imprint","IMPRINT",FACE,{"disambiguationData":[TD([[makeQuery(id+"F8.imprint","IMPRINT",EDGE,{"derivedFrom":sQuery(id+"F8.wireOp",EDGE,"E267.MirrorCS")}),-1.0]])]});
            extrude(context, id + "F9", {"entities" : qUnion([Q0]), "endBound" : BoundingType.SYMMETRIC, "depth" : 18.26 * mm});
        }
        {
            var Q0;
            Q0=sQuery(id+"F0.wireOp",EDGE,"E13");
            cPlane(context, id + "F10", {"entities" : qUnion([Q0]), "cplaneType" : CPlaneType.LINE_ANGLE, "offset" : 25.4 * mm, "angle" : 0 * degree, "width" : 152.4 * mm, "height" : 152.4 * mm});
        }
        {
            var Q0;
            Q0=qCreatedBy(id+"F10.planeOp",FACE);
            var sketch = newSketch(context, id + "F11", { "sketchPlane" : qUnion([Q0])});
            skLineSegment(sketch, "E307.MirrorCS", {"start": v(117.28, 387.35) * mm, "end": v(117.28, 405.61) * mm});
            skLineSegment(sketch, "E308.MirrorCS", {"start": v(117.28, 19.05) * mm, "end": v(117.28, 0) * mm});
            skLineSegment(sketch, "E309.MirrorCS", {"start": v(117.28, 0) * mm, "end": v(79.18, 0) * mm});
            skLineSegment(sketch, "E310.MirrorCS", {"start": v(41.09, 387.35) * mm, "end": v(50.61, 387.35) * mm});
            skLineSegment(sketch, "E311.MirrorCS", {"start": v(50.61, 405.61) * mm, "end": v(50.61, 387.35) * mm});
            skLineSegment(sketch, "E312.MirrorCS", {"start": v(79.18, 0) * mm, "end": v(79.18, 19.05) * mm});
            skLineSegment(sketch, "E313.MirrorCS", {"start": v(41.09, 387.35) * mm, "end": v(41.09, 373.26) * mm});
            skPoint(sketch, "E314.MirrorP", {"position": v(85.52, 0) * mm});
            skLineSegment(sketch, "E315.MirrorCS", {"start": v(-26.78, 139.13) * mm, "end": v(-27.27, 139.68) * mm});
            skLineSegment(sketch, "E316.MirrorCS", {"start": v(41.09, 373.26) * mm, "end": v(-147.09, 274.75) * mm});
            skPoint(sketch, "E317.MirrorP", {"position": v(117.28, 19.05) * mm});
            skLineSegment(sketch, "E318.MirrorCS", {"start": v(-16.37, 192.2) * mm, "end": v(-15.23, 197.99) * mm});
            skLineSegment(sketch, "E319.MirrorCS", {"start": v(-26.78, 139.13) * mm, "end": v(-26.75, 139.3) * mm});
            skLineSegment(sketch, "E320.trimOffspring", {"start": v(-27.27, 139.68) * mm, "end": v(-26.75, 139.3) * mm});
            skLineSegment(sketch, "E321", {"start": v(-307.67, 387.35) * mm, "end": v(-298.14, 387.35) * mm});
            skLineSegment(sketch, "E322", {"start": v(-371.17, 387.35) * mm, "end": v(-380.68, 387.35) * mm});
            skLineSegment(sketch, "E323", {"start": v(-298.14, 387.35) * mm, "end": v(-298.14, 369.53) * mm});
            skLineSegment(sketch, "E324", {"start": v(-371.17, 387.35) * mm, "end": v(-371.17, 405.61) * mm});
            skLineSegment(sketch, "E325", {"start": v(-307.67, 387.35) * mm, "end": v(-307.67, 405.61) * mm});
            skLineSegment(sketch, "E326", {"start": v(-380.68, 387.35) * mm, "end": v(-19.6, 141.35) * mm});
            skLineSegment(sketch, "E327.trimOffspring", {"start": v(-298.14, 369.53) * mm, "end": v(-160.13, 275.5) * mm});
            skPoint(sketch, "E328", {"position": v(-147.83, 267.12) * mm});
            skLineSegment(sketch, "E329", {"start": v(117.28, 19.05) * mm, "end": v(20, 143.25) * mm});
            skLineSegment(sketch, "E330.0", {"start": v(92.29, -0.53) * mm, "end": v(91.87, 0) * mm});
            skLineSegment(sketch, "E331", {"start": v(79.18, 19.05) * mm, "end": v(76.95, 19.05) * mm});
            skLineSegment(sketch, "E332.trimOffspring", {"start": v(76.95, 19.05) * mm, "end": v(-16.76, 138.69) * mm});
            skLineSegment(sketch, "E333.0", {"start": v(117.28, 377.31) * mm, "end": v(40.1, 336.91) * mm});
            skLineSegment(sketch, "E334.trimOffspring", {"start": v(-106.59, 239.03) * mm, "end": v(-30.3, 187.05) * mm});
            skPoint(sketch, "E335.orphan", {"position": v(-307.67, 376.03) * mm});
            skLineSegment(sketch, "E336", {"start": v(117.28, 377.31) * mm, "end": v(117.28, 387.35) * mm});
            skLineSegment(sketch, "E337", {"start": v(17.34, 152.24) * mm, "end": v(33.35, 326.82) * mm});
            skLineSegment(sketch, "E338.0", {"start": v(-10.5, 196.38) * mm, "end": v(-1.64, 292.94) * mm});
            skLineSegment(sketch, "E339.trimOffspring", {"start": v(-20.18, 305.35) * mm, "end": v(-105.33, 260.78) * mm});
            skPoint(sketch, "E340.trimOffspring.end.orphan", {"position": v(12.02, 158.22) * mm});
            skPoint(sketch, "E341.orphan", {"position": v(-161.66, 267.12) * mm});
            skPoint(sketch, "E342.visualSharp", {"position": v(-124.1, 250.95) * mm});
            skArc(sketch, "E342.filletArc", {"start": v(-105.33, 260.78) * mm, "mid": v(-112.12, 250.26) * mm, "end": v(-106.59, 239.03) * mm});
            skPoint(sketch, "E343.visualSharp", {"position": v(0.49, 316.17) * mm});
            skArc(sketch, "E343.filletArc", {"start": v(-1.64, 292.94) * mm, "mid": v(-7.22, 304.65) * mm, "end": v(-20.18, 305.35) * mm});
            skPoint(sketch, "E344.visualSharp", {"position": v(-12.46, 174.9) * mm});
            skArc(sketch, "E344.filletArc", {"start": v(-30.3, 187.05) * mm, "mid": v(-17.72, 186.06) * mm, "end": v(-10.5, 196.38) * mm});
            skPoint(sketch, "E345.visualSharp", {"position": v(-17.98, 140.24) * mm});
            skArc(sketch, "E345.filletArc", {"start": v(-16.76, 138.69) * mm, "mid": v(-18.08, 140.13) * mm, "end": v(-19.6, 141.35) * mm});
            skPoint(sketch, "E346.visualSharp", {"position": v(-153.84, 271.22) * mm});
            skArc(sketch, "E346.filletArc", {"start": v(-160.13, 275.5) * mm, "mid": v(-153.71, 273.32) * mm, "end": v(-147.09, 274.75) * mm});
            skPoint(sketch, "E347.visualSharp", {"position": v(33.98, 333.7) * mm});
            skArc(sketch, "E347.filletArc", {"start": v(40.1, 336.91) * mm, "mid": v(35.44, 332.72) * mm, "end": v(33.35, 326.82) * mm});
            skPoint(sketch, "E348.visualSharp", {"position": v(16.88, 147.22) * mm});
            skArc(sketch, "E348.filletArc", {"start": v(17.34, 152.24) * mm, "mid": v(17.8, 147.5) * mm, "end": v(20, 143.25) * mm});
            skLineSegment(sketch, "E349", {"start": v(117.28, 405.61) * mm, "end": v(50.61, 405.61) * mm});
            skLineSegment(sketch, "E350.trimOffspring", {"start": v(-307.67, 405.61) * mm, "end": v(-371.17, 405.61) * mm});
            skSolve(sketch);
        }
        {
            var Q0;
            Q0=makeQuery(id+"F11.imprint","IMPRINT",FACE,{"disambiguationData":[TD([[makeQuery(id+"F11.imprint","IMPRINT",EDGE,{"derivedFrom":sQuery(id+"F11.wireOp",EDGE,"E316.MirrorCS")}),1.0]])]});
            extrude(context, id + "F12", {"entities" : qUnion([Q0]), "endBound" : BoundingType.SYMMETRIC, "depth" : 18.26 * mm});
        }
        {
            var Q0;
            Q0=makeQuery(id+"F0.imprint","IMPRINT",FACE,{"disambiguationData":[TD([[makeQuery(id+"F0.imprint","IMPRINT",EDGE,{"derivedFrom":sQuery(id+"F0.wireOp",EDGE,"E91")}),-1.0]])]});
            extrude(context, id + "F13", {"entities" : qUnion([Q0]), "depth" : 19.05 * mm});
        }
        {
            var Q0;
            Q0=sQuery(id+"F0.wireOp",EDGE,"E14");
            cPlane(context, id + "F14", {"entities" : qUnion([Q0]), "cplaneType" : CPlaneType.LINE_ANGLE, "offset" : 25.4 * mm, "angle" : 0 * degree, "width" : 152.4 * mm, "height" : 152.4 * mm});
        }
        {
            var Q0;
            Q0=qCreatedBy(id+"F14.planeOp",FACE);
            var sketch = newSketch(context, id + "F15", { "sketchPlane" : qUnion([Q0])});
            skLineSegment(sketch, "E351.MirrorCS", {"start": v(1180.18, 19.05) * mm, "end": v(1180.18, 0) * mm});
            skLineSegment(sketch, "E352.MirrorCS", {"start": v(1180.18, 0) * mm, "end": v(1142.08, 0) * mm});
            skLineSegment(sketch, "E353.MirrorCS", {"start": v(1103.99, 387.35) * mm, "end": v(1113.51, 387.35) * mm});
            skLineSegment(sketch, "E354.MirrorCS", {"start": v(1142.08, 0) * mm, "end": v(1142.08, 19.05) * mm});
            skLineSegment(sketch, "E355.MirrorCS", {"start": v(1103.99, 387.35) * mm, "end": v(1103.99, 373.26) * mm});
            skPoint(sketch, "E356.MirrorP", {"position": v(1148.42, 0) * mm});
            skLineSegment(sketch, "E357.MirrorCS", {"start": v(1036.12, 139.13) * mm, "end": v(1035.64, 139.68) * mm});
            skLineSegment(sketch, "E358.MirrorCS", {"start": v(1103.99, 373.26) * mm, "end": v(915.81, 274.75) * mm});
            skPoint(sketch, "E359.MirrorP", {"position": v(1180.18, 19.05) * mm});
            skLineSegment(sketch, "E360.MirrorCS", {"start": v(1046.53, 192.2) * mm, "end": v(1047.67, 197.99) * mm});
            skLineSegment(sketch, "E361.MirrorCS", {"start": v(1036.12, 139.13) * mm, "end": v(1036.15, 139.3) * mm});
            skLineSegment(sketch, "E362.trimOffspring", {"start": v(1035.64, 139.68) * mm, "end": v(1036.15, 139.3) * mm});
            skLineSegment(sketch, "E363", {"start": v(755.23, 387.35) * mm, "end": v(764.76, 387.35) * mm});
            skLineSegment(sketch, "E364", {"start": v(691.73, 387.35) * mm, "end": v(682.22, 387.35) * mm});
            skLineSegment(sketch, "E365", {"start": v(764.76, 387.35) * mm, "end": v(764.76, 369.53) * mm});
            skLineSegment(sketch, "E366", {"start": v(691.73, 387.35) * mm, "end": v(691.73, 405.61) * mm});
            skLineSegment(sketch, "E367", {"start": v(755.23, 387.35) * mm, "end": v(755.23, 405.61) * mm});
            skLineSegment(sketch, "E368", {"start": v(682.22, 387.35) * mm, "end": v(1043.3, 141.35) * mm});
            skLineSegment(sketch, "E369.trimOffspring", {"start": v(764.76, 369.53) * mm, "end": v(902.77, 275.5) * mm});
            skPoint(sketch, "E370", {"position": v(915.07, 267.12) * mm});
            skLineSegment(sketch, "E371", {"start": v(1180.18, 19.05) * mm, "end": v(1082.9, 143.25) * mm});
            skLineSegment(sketch, "E372.0", {"start": v(1155.19, -0.53) * mm, "end": v(1154.77, 0) * mm});
            skLineSegment(sketch, "E373", {"start": v(1142.08, 19.05) * mm, "end": v(1139.85, 19.05) * mm});
            skLineSegment(sketch, "E374.trimOffspring", {"start": v(1139.85, 19.05) * mm, "end": v(1046.14, 138.69) * mm});
            skLineSegment(sketch, "E375.0", {"start": v(1180.18, 377.31) * mm, "end": v(1103, 336.91) * mm});
            skLineSegment(sketch, "E376.trimOffspring", {"start": v(956.31, 239.03) * mm, "end": v(1032.6, 187.05) * mm});
            skLineSegment(sketch, "E377", {"start": v(1180.18, 377.31) * mm, "end": v(1180.18, 405.61) * mm});
            skLineSegment(sketch, "E378", {"start": v(1080.24, 152.24) * mm, "end": v(1096.25, 326.82) * mm});
            skLineSegment(sketch, "E379.0", {"start": v(1052.4, 196.38) * mm, "end": v(1061.26, 292.94) * mm});
            skLineSegment(sketch, "E380.trimOffspring", {"start": v(1042.72, 305.35) * mm, "end": v(957.57, 260.77) * mm});
            skPoint(sketch, "E381.trimOffspring.end.orphan", {"position": v(1074.92, 158.22) * mm});
            skPoint(sketch, "E382.orphan", {"position": v(901.24, 267.12) * mm});
            skPoint(sketch, "E383.visualSharp", {"position": v(938.8, 250.95) * mm});
            skArc(sketch, "E383.filletArc", {"start": v(957.57, 260.77) * mm, "mid": v(950.78, 250.26) * mm, "end": v(956.31, 239.03) * mm});
            skPoint(sketch, "E384.visualSharp", {"position": v(1063.39, 316.17) * mm});
            skArc(sketch, "E384.filletArc", {"start": v(1061.26, 292.94) * mm, "mid": v(1055.68, 304.65) * mm, "end": v(1042.72, 305.35) * mm});
            skPoint(sketch, "E385.visualSharp", {"position": v(1050.44, 174.9) * mm});
            skArc(sketch, "E385.filletArc", {"start": v(1032.6, 187.05) * mm, "mid": v(1045.18, 186.05) * mm, "end": v(1052.4, 196.38) * mm});
            skPoint(sketch, "E386.visualSharp", {"position": v(1044.92, 140.24) * mm});
            skArc(sketch, "E386.filletArc", {"start": v(1046.14, 138.69) * mm, "mid": v(1044.82, 140.13) * mm, "end": v(1043.3, 141.35) * mm});
            skPoint(sketch, "E387.visualSharp", {"position": v(909.06, 271.22) * mm});
            skArc(sketch, "E387.filletArc", {"start": v(902.77, 275.5) * mm, "mid": v(909.19, 273.32) * mm, "end": v(915.81, 274.75) * mm});
            skPoint(sketch, "E388.visualSharp", {"position": v(1096.88, 333.7) * mm});
            skArc(sketch, "E388.filletArc", {"start": v(1103, 336.91) * mm, "mid": v(1098.34, 332.72) * mm, "end": v(1096.25, 326.82) * mm});
            skPoint(sketch, "E389.visualSharp", {"position": v(1079.78, 147.22) * mm});
            skArc(sketch, "E389.filletArc", {"start": v(1080.24, 152.24) * mm, "mid": v(1080.7, 147.5) * mm, "end": v(1082.9, 143.25) * mm});
            skLineSegment(sketch, "E390", {"start": v(1180.18, 405.61) * mm, "end": v(1113.51, 405.61) * mm});
            skLineSegment(sketch, "E391.trimOffspring", {"start": v(755.23, 405.61) * mm, "end": v(691.73, 405.61) * mm});
            skLineSegment(sketch, "E392", {"start": v(1113.51, 405.61) * mm, "end": v(1113.51, 387.35) * mm});
            skSolve(sketch);
        }
        {
            var Q0;
            Q0=makeQuery(id+"F15.imprint","IMPRINT",FACE,{"disambiguationData":[TD([[makeQuery(id+"F15.imprint","IMPRINT",EDGE,{"derivedFrom":sQuery(id+"F15.wireOp",EDGE,"E358.MirrorCS")}),1.0]])]});
            extrude(context, id + "F16", {"entities" : qUnion([Q0]), "endBound" : BoundingType.SYMMETRIC, "depth" : 18.26 * mm});
        }
        {
            var Q0;
            Q0=sQuery(id+"F0.wireOp",EDGE,"E166");
            cPlane(context, id + "F17", {"entities" : qUnion([Q0]), "cplaneType" : CPlaneType.LINE_ANGLE, "offset" : 25.4 * mm, "angle" : 90 * degree, "width" : 152.4 * mm, "height" : 152.4 * mm});
        }
        {
            var Q0;
            Q0=qCreatedBy(id+"F17.planeOp",FACE);
            var sketch = newSketch(context, id + "F18", { "sketchPlane" : qUnion([Q0])});
            skLineSegment(sketch, "E393.MirrorCS", {"start": v(761.7, 387.35) * mm, "end": v(771.22, 387.35) * mm});
            skLineSegment(sketch, "E394.MirrorCS", {"start": v(837.9, 387.35) * mm, "end": v(828.37, 387.35) * mm});
            skLineSegment(sketch, "E395.MirrorCS", {"start": v(1048.59, 387.35) * mm, "end": v(1058.11, 387.35) * mm});
            skLineSegment(sketch, "E396.MirrorCS", {"start": v(1124.78, 387.35) * mm, "end": v(1124.78, 405.61) * mm});
            skLineSegment(sketch, "E397.MirrorCS", {"start": v(1124.78, 19.05) * mm, "end": v(1124.78, 0) * mm});
            skLineSegment(sketch, "E398.MirrorCS", {"start": v(1048.59, 387.35) * mm, "end": v(1048.59, 377.45) * mm});
            skPoint(sketch, "E399.MirrorP", {"position": v(1124.78, 19.05) * mm});
            skLineSegment(sketch, "E400.MirrorCS", {"start": v(1086.68, 0) * mm, "end": v(1086.68, 19.05) * mm});
            skLineSegment(sketch, "E401.MirrorCS", {"start": v(1058.11, 405.61) * mm, "end": v(1058.11, 387.35) * mm});
            skLineSegment(sketch, "E402.MirrorCS", {"start": v(882, 286.35) * mm, "end": v(828.18, 345.6) * mm});
            skLineSegment(sketch, "E403.MirrorCS", {"start": v(1124.78, 0) * mm, "end": v(1086.68, 0) * mm});
            skLineSegment(sketch, "E404.MirrorCS", {"start": v(968.37, 191.26) * mm, "end": v(921.07, 243.33) * mm});
            skLineSegment(sketch, "E405.MirrorCS", {"start": v(1124.78, 19.05) * mm, "end": v(1013.2, 141.9) * mm});
            skPoint(sketch, "E406.MirrorP", {"position": v(1093.02, 0) * mm});
            skLineSegment(sketch, "E407.MirrorCS", {"start": v(761.7, 371.58) * mm, "end": v(761.7, 387.35) * mm});
            skLineSegment(sketch, "E408.MirrorCS", {"start": v(828.37, 387.35) * mm, "end": v(828.37, 405.61) * mm});
            skLineSegment(sketch, "E409.MirrorCS", {"start": v(1124.78, 387.35) * mm, "end": v(1074.58, 356.2) * mm});
            skLineSegment(sketch, "E410.MirrorCS", {"start": v(771.22, 387.35) * mm, "end": v(771.22, 405.61) * mm});
            skLineSegment(sketch, "E411.MirrorCS", {"start": v(1001.2, 310.69) * mm, "end": v(923.78, 262.66) * mm});
            skLineSegment(sketch, "E412.0", {"start": v(1081.89, 19.05) * mm, "end": v(761.7, 371.58) * mm});
            skLineSegment(sketch, "E413", {"start": v(1081.89, 19.05) * mm, "end": v(1086.68, 19.05) * mm});
            skLineSegment(sketch, "E414.0", {"start": v(1048.59, 377.45) * mm, "end": v(898.1, 284.1) * mm});
            skLineSegment(sketch, "E415", {"start": v(837.9, 371.58) * mm, "end": v(837.9, 387.35) * mm});
            skLineSegment(sketch, "E416", {"start": v(837.9, 371.58) * mm, "end": v(829.05, 363.54) * mm});
            skLineSegment(sketch, "E417", {"start": v(1069.11, 349.08) * mm, "end": v(1010.44, 154.1) * mm});
            skLineSegment(sketch, "E418.0", {"start": v(1020.05, 296.24) * mm, "end": v(989.93, 196.14) * mm});
            skPoint(sketch, "E419.visualSharp", {"position": v(889.11, 278.52) * mm});
            skArc(sketch, "E419.filletArc", {"start": v(882, 286.35) * mm, "mid": v(889.64, 282.3) * mm, "end": v(898.1, 284.1) * mm});
            skPoint(sketch, "E420.visualSharp", {"position": v(1029.73, 328.39) * mm});
            skArc(sketch, "E420.filletArc", {"start": v(1020.05, 296.24) * mm, "mid": v(1015.62, 309.98) * mm, "end": v(1001.2, 310.69) * mm});
            skPoint(sketch, "E421.visualSharp", {"position": v(983.46, 174.64) * mm});
            skArc(sketch, "E421.filletArc", {"start": v(968.37, 191.26) * mm, "mid": v(980.57, 187.41) * mm, "end": v(989.93, 196.14) * mm});
            skPoint(sketch, "E422.visualSharp", {"position": v(910.82, 254.62) * mm});
            skArc(sketch, "E422.filletArc", {"start": v(923.78, 262.66) * mm, "mid": v(917.9, 253.63) * mm, "end": v(921.07, 243.33) * mm});
            skPoint(sketch, "E423.visualSharp", {"position": v(1008.37, 147.22) * mm});
            skArc(sketch, "E423.filletArc", {"start": v(1010.44, 154.1) * mm, "mid": v(1010.21, 147.64) * mm, "end": v(1013.2, 141.9) * mm});
            skPoint(sketch, "E424.visualSharp", {"position": v(819.65, 355) * mm});
            skArc(sketch, "E424.filletArc", {"start": v(829.05, 363.54) * mm, "mid": v(824.9, 354.75) * mm, "end": v(828.18, 345.6) * mm});
            skPoint(sketch, "E425.visualSharp", {"position": v(1070.5, 353.68) * mm});
            skArc(sketch, "E425.filletArc", {"start": v(1074.58, 356.2) * mm, "mid": v(1071.2, 353.14) * mm, "end": v(1069.11, 349.08) * mm});
            skLineSegment(sketch, "E426.0", {"start": v(790.44, 405.61) * mm, "end": v(790.44, 381) * mm});
            skLineSegment(sketch, "E427.0", {"start": v(809.16, 405.61) * mm, "end": v(809.16, 381) * mm});
            skLineSegment(sketch, "E428", {"start": v(790.44, 381) * mm, "end": v(809.16, 381) * mm});
            skLineSegment(sketch, "E429", {"start": v(771.22, 405.61) * mm, "end": v(790.44, 405.61) * mm});
            skLineSegment(sketch, "E430.trimOffspring", {"start": v(1058.11, 405.61) * mm, "end": v(1124.78, 405.61) * mm});
            skLineSegment(sketch, "E431.trimOffspring", {"start": v(809.16, 405.61) * mm, "end": v(828.37, 405.61) * mm});
            skSolve(sketch);
        }
        {
            var Q0;
            {var subQ4=sQuery(id+"F18.wireOp",EDGE,"E393.MirrorCS");Q0=makeQuery(id+"F18.imprint","IMPRINT",FACE,{"disambiguationData":[TD([[makeQuery(id+"F18.imprint","IMPRINT",EDGE,{"derivedFrom":subQ4}),-1.0]])]});}
            extrude(context, id + "F19", {"entities" : qUnion([Q0]), "endBound" : BoundingType.SYMMETRIC, "depth" : 18.26 * mm});
        }
        {
            var Q0;
            Q0=sQuery(id+"F0.wireOp",EDGE,"E154");
            cPlane(context, id + "F20", {"entities" : qUnion([Q0]), "cplaneType" : CPlaneType.LINE_ANGLE, "offset" : 25.4 * mm, "angle" : 90 * degree, "width" : 152.4 * mm, "height" : 152.4 * mm});
        }
        {
            var Q0;
            Q0=qCreatedBy(id+"F20.planeOp",FACE);
            var sketch = newSketch(context, id + "F21", { "sketchPlane" : qUnion([Q0])});
            skLineSegment(sketch, "E432.MirrorCS", {"start": v(-414.01, 380.97) * mm, "end": v(-395.3, 380.97) * mm});
            skLineSegment(sketch, "E433.MirrorCS", {"start": v(-441.6, 387.35) * mm, "end": v(-432.08, 387.35) * mm});
            skArc(sketch, "E434.MirrorCS", {"start": v(-678.28, 356.2) * mm, "mid": v(-674.9, 353.14) * mm, "end": v(-672.82, 349.08) * mm});
            skArc(sketch, "E435.MirrorCS", {"start": v(-614.14, 154.1) * mm, "mid": v(-613.92, 147.64) * mm, "end": v(-616.9, 141.9) * mm});
            skLineSegment(sketch, "E436.MirrorCS", {"start": v(-441.6, 371.58) * mm, "end": v(-432.75, 363.54) * mm});
            skLineSegment(sketch, "E437.MirrorCS", {"start": v(-728.48, 19.05) * mm, "end": v(-728.48, 0) * mm});
            skLineSegment(sketch, "E438.MirrorCS", {"start": v(-365.4, 387.35) * mm, "end": v(-374.93, 387.35) * mm});
            skLineSegment(sketch, "E439.MirrorCS", {"start": v(-441.6, 371.58) * mm, "end": v(-441.6, 387.35) * mm});
            skLineSegment(sketch, "E440.MirrorCS", {"start": v(-728.48, 387.35) * mm, "end": v(-728.48, 405.61) * mm});
            skArc(sketch, "E441.MirrorCS", {"start": v(-485.7, 286.35) * mm, "mid": v(-493.35, 282.3) * mm, "end": v(-501.8, 284.1) * mm});
            skArc(sketch, "E442.MirrorCS", {"start": v(-572.07, 191.26) * mm, "mid": v(-584.28, 187.41) * mm, "end": v(-593.64, 196.14) * mm});
            skLineSegment(sketch, "E443.MirrorCS", {"start": v(-432.08, 387.35) * mm, "end": v(-432.08, 405.61) * mm});
            skLineSegment(sketch, "E444.MirrorCS", {"start": v(-374.93, 387.35) * mm, "end": v(-374.93, 405.61) * mm});
            skArc(sketch, "E445.MirrorCS", {"start": v(-432.75, 363.54) * mm, "mid": v(-428.6, 354.75) * mm, "end": v(-431.89, 345.6) * mm});
            skArc(sketch, "E446.MirrorCS", {"start": v(-527.49, 262.66) * mm, "mid": v(-521.6, 253.63) * mm, "end": v(-524.78, 243.33) * mm});
            skLineSegment(sketch, "E447.MirrorCS", {"start": v(-652.3, 387.35) * mm, "end": v(-652.3, 377.45) * mm});
            skLineSegment(sketch, "E448.MirrorCS", {"start": v(-652.3, 387.35) * mm, "end": v(-661.82, 387.35) * mm});
            skLineSegment(sketch, "E449.MirrorCS", {"start": v(-690.38, 0) * mm, "end": v(-690.38, 19.05) * mm});
            skLineSegment(sketch, "E450.MirrorCS", {"start": v(-685.6, 19.05) * mm, "end": v(-690.38, 19.05) * mm});
            skLineSegment(sketch, "E451.MirrorCS", {"start": v(-661.82, 405.61) * mm, "end": v(-661.82, 387.35) * mm});
            skArc(sketch, "E452.MirrorCS", {"start": v(-623.76, 296.24) * mm, "mid": v(-619.32, 309.98) * mm, "end": v(-604.9, 310.69) * mm});
            skPoint(sketch, "E453.MirrorP", {"position": v(-514.52, 254.62) * mm});
            skPoint(sketch, "E454.MirrorP", {"position": v(-612.07, 147.22) * mm});
            skPoint(sketch, "E455.MirrorP", {"position": v(-423.35, 355) * mm});
            skPoint(sketch, "E456.MirrorP", {"position": v(-674.2, 353.68) * mm});
            skPoint(sketch, "E457.MirrorP", {"position": v(-696.72, 0) * mm});
            skPoint(sketch, "E458.MirrorP", {"position": v(-728.48, 19.05) * mm});
            skLineSegment(sketch, "E459.MirrorCS", {"start": v(-728.48, 19.05) * mm, "end": v(-616.9, 141.9) * mm});
            skLineSegment(sketch, "E460.MirrorCS", {"start": v(-672.82, 349.08) * mm, "end": v(-614.14, 154.1) * mm});
            skLineSegment(sketch, "E461.MirrorCS", {"start": v(-604.9, 310.69) * mm, "end": v(-527.49, 262.66) * mm});
            skLineSegment(sketch, "E462.MirrorCS", {"start": v(-685.6, 19.05) * mm, "end": v(-414.01, 318.06) * mm});
            skPoint(sketch, "E463.MirrorP", {"position": v(-492.82, 278.52) * mm});
            skPoint(sketch, "E464.MirrorP", {"position": v(-633.44, 328.39) * mm});
            skLineSegment(sketch, "E465.MirrorCS", {"start": v(-485.7, 286.35) * mm, "end": v(-431.89, 345.6) * mm});
            skLineSegment(sketch, "E466.MirrorCS", {"start": v(-728.48, 0) * mm, "end": v(-690.38, 0) * mm});
            skLineSegment(sketch, "E467.MirrorCS", {"start": v(-652.3, 377.45) * mm, "end": v(-501.8, 284.1) * mm});
            skLineSegment(sketch, "E468.MirrorCS", {"start": v(-623.76, 296.24) * mm, "end": v(-593.64, 196.14) * mm});
            skLineSegment(sketch, "E469.MirrorCS", {"start": v(-572.07, 191.26) * mm, "end": v(-524.78, 243.33) * mm});
            skLineSegment(sketch, "E470.MirrorCS", {"start": v(-728.48, 387.35) * mm, "end": v(-678.28, 356.2) * mm});
            skPoint(sketch, "E471.MirrorP", {"position": v(-314.43, 209.55) * mm});
            skPoint(sketch, "E472.MirrorP", {"position": v(-587.17, 174.64) * mm});
            skLineSegment(sketch, "E473.MirrorCS", {"start": v(-365.4, 371.58) * mm, "end": v(-365.4, 387.35) * mm});
            skLineSegment(sketch, "E474.trimOffspring", {"start": v(-395.3, 338.67) * mm, "end": v(-365.4, 371.58) * mm});
            skLineSegment(sketch, "E475.0", {"start": v(-395.3, 387.35) * mm, "end": v(-395.3, 387.35) * mm});
            skLineSegment(sketch, "E476.0", {"start": v(-414.01, 387.35) * mm, "end": v(-414.01, 387.35) * mm});
            skLineSegment(sketch, "E477.trimOffspring", {"start": v(-414.01, 380.97) * mm, "end": v(-414.01, 318.06) * mm});
            skLineSegment(sketch, "E478.trimOffspring", {"start": v(-395.3, 380.97) * mm, "end": v(-395.3, 338.67) * mm});
            skLineSegment(sketch, "E479", {"start": v(-728.48, 405.61) * mm, "end": v(-661.82, 405.61) * mm});
            skLineSegment(sketch, "E480.trimOffspring", {"start": v(-432.08, 405.61) * mm, "end": v(-374.93, 405.61) * mm});
            skSolve(sketch);
        }
        {
            var Q0;
            Q0=makeQuery(id+"F21.imprint","IMPRINT",FACE,{"disambiguationData":[TD([[makeQuery(id+"F21.imprint","IMPRINT",EDGE,{"derivedFrom":sQuery(id+"F21.wireOp",EDGE,"E433.MirrorCS")}),-1.0]])]});
            extrude(context, id + "F22", {"entities" : qUnion([Q0]), "endBound" : BoundingType.SYMMETRIC, "depth" : 18.26 * mm});
        }
        {
            var Q0;
            Q0=sQuery(id+"F0.wireOp",EDGE,"E15");
            cPlane(context, id + "F23", {"entities" : qUnion([Q0]), "cplaneType" : CPlaneType.LINE_ANGLE, "offset" : 25.4 * mm, "angle" : 0 * degree, "width" : 152.4 * mm, "height" : 152.4 * mm});
        }
        {
            var Q0;
            Q0=qCreatedBy(id+"F23.planeOp",FACE);
            var sketch = newSketch(context, id + "F24", { "sketchPlane" : qUnion([Q0])});
            skLineSegment(sketch, "E481.MirrorCS", {"start": v(1007.5, 19.05) * mm, "end": v(1007.5, 0) * mm});
            skLineSegment(sketch, "E482.MirrorCS", {"start": v(1007.5, 0) * mm, "end": v(969.4, 0) * mm});
            skLineSegment(sketch, "E483.MirrorCS", {"start": v(931.3, 387.35) * mm, "end": v(940.83, 387.35) * mm});
            skLineSegment(sketch, "E484.MirrorCS", {"start": v(969.4, 0) * mm, "end": v(969.4, 19.05) * mm});
            skLineSegment(sketch, "E485.MirrorCS", {"start": v(931.3, 387.35) * mm, "end": v(931.3, 373.26) * mm});
            skPoint(sketch, "E486.MirrorP", {"position": v(975.74, 0) * mm});
            skLineSegment(sketch, "E487.MirrorCS", {"start": v(863.44, 139.13) * mm, "end": v(862.96, 139.68) * mm});
            skLineSegment(sketch, "E488.MirrorCS", {"start": v(931.3, 373.26) * mm, "end": v(743.13, 274.75) * mm});
            skPoint(sketch, "E489.MirrorP", {"position": v(1007.5, 19.05) * mm});
            skLineSegment(sketch, "E490.MirrorCS", {"start": v(873.86, 192.2) * mm, "end": v(875, 197.99) * mm});
            skLineSegment(sketch, "E491.MirrorCS", {"start": v(863.44, 139.13) * mm, "end": v(863.47, 139.3) * mm});
            skLineSegment(sketch, "E492.MirrorCS", {"start": v(940.83, 405.61) * mm, "end": v(940.83, 387.35) * mm});
            skLineSegment(sketch, "E493.trimOffspring", {"start": v(862.96, 139.68) * mm, "end": v(863.47, 139.3) * mm});
            skLineSegment(sketch, "E494", {"start": v(582.55, 387.35) * mm, "end": v(592.09, 387.35) * mm});
            skLineSegment(sketch, "E495", {"start": v(519.05, 387.35) * mm, "end": v(509.54, 387.35) * mm});
            skLineSegment(sketch, "E496", {"start": v(592.09, 387.35) * mm, "end": v(592.09, 369.53) * mm});
            skLineSegment(sketch, "E497", {"start": v(519.05, 387.35) * mm, "end": v(519.05, 405.61) * mm});
            skLineSegment(sketch, "E498", {"start": v(582.55, 387.35) * mm, "end": v(582.55, 405.61) * mm});
            skLineSegment(sketch, "E499", {"start": v(509.54, 387.35) * mm, "end": v(870.61, 141.35) * mm});
            skLineSegment(sketch, "E500.trimOffspring", {"start": v(592.09, 369.53) * mm, "end": v(730.1, 275.5) * mm});
            skPoint(sketch, "E501", {"position": v(742.4, 267.12) * mm});
            skLineSegment(sketch, "E502", {"start": v(1007.5, 19.05) * mm, "end": v(910.21, 143.25) * mm});
            skLineSegment(sketch, "E503.0", {"start": v(982.5, -0.53) * mm, "end": v(982.1, 0) * mm});
            skLineSegment(sketch, "E504", {"start": v(969.4, 19.05) * mm, "end": v(967.17, 19.05) * mm});
            skLineSegment(sketch, "E505.trimOffspring", {"start": v(967.17, 19.05) * mm, "end": v(873.46, 138.69) * mm});
            skLineSegment(sketch, "E506.0", {"start": v(1007.5, 377.31) * mm, "end": v(930.33, 336.91) * mm});
            skLineSegment(sketch, "E507.trimOffspring", {"start": v(783.63, 239.03) * mm, "end": v(859.93, 187.05) * mm});
            skLineSegment(sketch, "E508", {"start": v(1007.5, 377.31) * mm, "end": v(1007.5, 405.61) * mm});
            skLineSegment(sketch, "E509", {"start": v(907.57, 152.24) * mm, "end": v(923.57, 326.82) * mm});
            skLineSegment(sketch, "E510.0", {"start": v(879.73, 196.38) * mm, "end": v(888.58, 292.94) * mm});
            skLineSegment(sketch, "E511.trimOffspring", {"start": v(870.04, 305.35) * mm, "end": v(784.9, 260.77) * mm});
            skPoint(sketch, "E512.trimOffspring.end.orphan", {"position": v(902.24, 158.22) * mm});
            skPoint(sketch, "E513.orphan", {"position": v(728.56, 267.12) * mm});
            skPoint(sketch, "E514.visualSharp", {"position": v(766.13, 250.95) * mm});
            skArc(sketch, "E514.filletArc", {"start": v(784.9, 260.77) * mm, "mid": v(778.1, 250.26) * mm, "end": v(783.63, 239.03) * mm});
            skPoint(sketch, "E515.visualSharp", {"position": v(890.7, 316.17) * mm});
            skArc(sketch, "E515.filletArc", {"start": v(888.58, 292.94) * mm, "mid": v(883, 304.65) * mm, "end": v(870.04, 305.35) * mm});
            skPoint(sketch, "E516.visualSharp", {"position": v(877.76, 174.9) * mm});
            skArc(sketch, "E516.filletArc", {"start": v(859.93, 187.05) * mm, "mid": v(872.5, 186.05) * mm, "end": v(879.73, 196.38) * mm});
            skPoint(sketch, "E517.visualSharp", {"position": v(872.24, 140.24) * mm});
            skArc(sketch, "E517.filletArc", {"start": v(873.46, 138.69) * mm, "mid": v(872.14, 140.13) * mm, "end": v(870.61, 141.35) * mm});
            skPoint(sketch, "E518.visualSharp", {"position": v(736.38, 271.22) * mm});
            skArc(sketch, "E518.filletArc", {"start": v(730.1, 275.5) * mm, "mid": v(736.5, 273.32) * mm, "end": v(743.13, 274.75) * mm});
            skPoint(sketch, "E519.visualSharp", {"position": v(924.2, 333.7) * mm});
            skArc(sketch, "E519.filletArc", {"start": v(930.33, 336.91) * mm, "mid": v(925.66, 332.72) * mm, "end": v(923.57, 326.82) * mm});
            skPoint(sketch, "E520.visualSharp", {"position": v(907.1, 147.22) * mm});
            skArc(sketch, "E520.filletArc", {"start": v(907.57, 152.24) * mm, "mid": v(908.03, 147.5) * mm, "end": v(910.21, 143.25) * mm});
            skLineSegment(sketch, "E521", {"start": v(519.05, 405.61) * mm, "end": v(582.55, 405.61) * mm});
            skLineSegment(sketch, "E522.trimOffspring", {"start": v(940.83, 405.61) * mm, "end": v(1007.5, 405.61) * mm});
            skSolve(sketch);
        }
        {
            var Q0;
            Q0=makeQuery(id+"F24.imprint","IMPRINT",FACE,{"disambiguationData":[TD([[makeQuery(id+"F24.imprint","IMPRINT",EDGE,{"derivedFrom":sQuery(id+"F24.wireOp",EDGE,"E488.MirrorCS")}),1.0]])]});
            extrude(context, id + "F25", {"entities" : qUnion([Q0]), "endBound" : BoundingType.SYMMETRIC, "depth" : 18.26 * mm});
        }
        {
            var Q0;
            Q0=makeQuery(id+"F3.opExtrude","SWEPT_FACE",FACE,{"disambiguationData":[OSD([sQuery(id+"F2.wireOp",EDGE,"E193")])]});
            cPlane(context, id + "F26", {"entities" : qUnion([Q0]), "cplaneType" : CPlaneType.OFFSET, "offset" : 0 * mm, "width" : 152.4 * mm, "height" : 152.4 * mm});
        }
        {
            var Q0;
            Q0=qCreatedBy(id+"F26.planeOp",FACE);
            var sketch = newSketch(context, id + "F27", { "sketchPlane" : qUnion([Q0])});
            skLineSegment(sketch, "E523.bottom", {"start": v(24.81, 15.08) * mm, "end": v(1083.76, 15.08) * mm, "construction": true});
            skLineSegment(sketch, "E523.top", {"start": v(24.81, 543.61) * mm, "end": v(1083.84, 543.61) * mm, "construction": true});
            skLineSegment(sketch, "E523.right", {"start": v(1083.76, 15.08) * mm, "end": v(1083.84, 543.61) * mm, "construction": true});
            skLineSegment(sketch, "E524", {"start": v(24.81, 15.08) * mm, "end": v(24.81, 543.61) * mm, "construction": true});
            skPoint(sketch, "E525", {"position": v(20.81, 537.06) * mm});
            skLineSegment(sketch, "E526.0", {"start": v(42.6, 515.98) * mm, "end": v(29.35, 502.74) * mm});
            skLineSegment(sketch, "E526.1", {"start": v(42.6, 515.98) * mm, "end": v(90.05, 468.51) * mm});
            skLineSegment(sketch, "E526.2", {"start": v(90.05, 468.51) * mm, "end": v(76.82, 455.28) * mm});
            skLineSegment(sketch, "E526.3", {"start": v(29.35, 502.74) * mm, "end": v(76.82, 455.28) * mm});
            skLineSegment(sketch, "E527.0", {"start": v(45.8, 521.22) * mm, "end": v(109.64, 500.47) * mm});
            skLineSegment(sketch, "E527.1", {"start": v(51.58, 539.02) * mm, "end": v(45.8, 521.22) * mm});
            skLineSegment(sketch, "E527.2", {"start": v(51.58, 539.02) * mm, "end": v(115.42, 518.28) * mm});
            skLineSegment(sketch, "E527.3", {"start": v(115.42, 518.28) * mm, "end": v(109.64, 500.47) * mm});
            skLineSegment(sketch, "E528.0", {"start": v(252.18, 252.41) * mm, "end": v(265.93, 266.16) * mm});
            skLineSegment(sketch, "E528.1", {"start": v(252.18, 252.41) * mm, "end": v(238.94, 265.65) * mm});
            skLineSegment(sketch, "E528.2", {"start": v(238.94, 265.65) * mm, "end": v(252.7, 279.4) * mm});
            skLineSegment(sketch, "E528.3", {"start": v(292.91, 293.15) * mm, "end": v(279.68, 306.38) * mm});
            skLineSegment(sketch, "E529.0", {"start": v(252.18, 306.39) * mm, "end": v(265.93, 292.64) * mm});
            skLineSegment(sketch, "E529.1", {"start": v(252.18, 306.39) * mm, "end": v(238.94, 293.15) * mm});
            skLineSegment(sketch, "E529.2", {"start": v(238.94, 293.15) * mm, "end": v(252.7, 279.4) * mm});
            skLineSegment(sketch, "E530.0", {"start": v(279.17, 279.4) * mm, "end": v(292.92, 265.65) * mm});
            skLineSegment(sketch, "E530.1", {"start": v(292.92, 265.65) * mm, "end": v(279.68, 252.41) * mm});
            skLineSegment(sketch, "E530.2", {"start": v(265.93, 266.16) * mm, "end": v(279.68, 252.41) * mm});
            skLineSegment(sketch, "E531.trimOffspring", {"start": v(265.93, 292.64) * mm, "end": v(279.68, 306.38) * mm});
            skLineSegment(sketch, "E532.trimOffspring", {"start": v(279.17, 279.4) * mm, "end": v(292.91, 293.15) * mm});
            skLineSegment(sketch, "E533.0", {"start": v(29.35, 56.06) * mm, "end": v(76.81, 103.52) * mm});
            skLineSegment(sketch, "E533.1", {"start": v(42.59, 42.82) * mm, "end": v(29.35, 56.06) * mm});
            skLineSegment(sketch, "E533.2", {"start": v(42.59, 42.82) * mm, "end": v(90.05, 90.29) * mm});
            skLineSegment(sketch, "E533.3", {"start": v(90.05, 90.29) * mm, "end": v(76.81, 103.52) * mm});
            skLineSegment(sketch, "E534.0", {"start": v(45.8, 37.58) * mm, "end": v(109.64, 58.32) * mm});
            skLineSegment(sketch, "E534.1", {"start": v(45.8, 37.58) * mm, "end": v(51.58, 19.78) * mm});
            skLineSegment(sketch, "E534.2", {"start": v(51.58, 19.78) * mm, "end": v(115.42, 40.52) * mm});
            skLineSegment(sketch, "E534.3", {"start": v(109.64, 58.32) * mm, "end": v(115.42, 40.52) * mm});
            skLineSegment(sketch, "E535.0", {"start": v(455.74, 151.1) * mm, "end": v(516.56, 170.86) * mm});
            skLineSegment(sketch, "E535.1", {"start": v(449.95, 168.9) * mm, "end": v(455.74, 151.1) * mm});
            skLineSegment(sketch, "E535.2", {"start": v(510.77, 188.66) * mm, "end": v(449.95, 168.9) * mm});
            skLineSegment(sketch, "E535.3", {"start": v(516.56, 170.86) * mm, "end": v(510.77, 188.66) * mm});
            skLineSegment(sketch, "E536.0", {"start": v(667.65, 168.9) * mm, "end": v(606.83, 188.66) * mm});
            skLineSegment(sketch, "E536.1", {"start": v(661.86, 151.1) * mm, "end": v(667.65, 168.9) * mm});
            skLineSegment(sketch, "E536.2", {"start": v(601.04, 170.86) * mm, "end": v(661.86, 151.1) * mm});
            skLineSegment(sketch, "E536.3", {"start": v(606.83, 188.66) * mm, "end": v(601.04, 170.86) * mm});
            skLineSegment(sketch, "E537.0", {"start": v(449.95, 389.9) * mm, "end": v(510.77, 370.14) * mm});
            skLineSegment(sketch, "E537.1", {"start": v(455.74, 407.7) * mm, "end": v(449.95, 389.9) * mm});
            skLineSegment(sketch, "E537.2", {"start": v(516.56, 387.94) * mm, "end": v(455.74, 407.7) * mm});
            skLineSegment(sketch, "E537.3", {"start": v(510.77, 370.14) * mm, "end": v(516.56, 387.94) * mm});
            skLineSegment(sketch, "E538.0", {"start": v(661.86, 407.7) * mm, "end": v(601.04, 387.94) * mm});
            skLineSegment(sketch, "E538.1", {"start": v(667.65, 389.9) * mm, "end": v(661.86, 407.7) * mm});
            skLineSegment(sketch, "E538.2", {"start": v(606.83, 370.14) * mm, "end": v(667.65, 389.9) * mm});
            skLineSegment(sketch, "E538.3", {"start": v(601.04, 387.94) * mm, "end": v(606.83, 370.14) * mm});
            skLineSegment(sketch, "E539.0", {"start": v(823.87, 293.96) * mm, "end": v(838.43, 279.4) * mm});
            skLineSegment(sketch, "E539.1", {"start": v(837.1, 307.2) * mm, "end": v(823.87, 293.96) * mm});
            skLineSegment(sketch, "E539.2", {"start": v(877.84, 266.47) * mm, "end": v(864.9, 279.4) * mm});
            skLineSegment(sketch, "E539.3", {"start": v(864.6, 253.23) * mm, "end": v(877.84, 266.47) * mm});
            skLineSegment(sketch, "E540.0", {"start": v(865.43, 306.4) * mm, "end": v(851.67, 292.64) * mm});
            skLineSegment(sketch, "E540.1", {"start": v(878.66, 293.16) * mm, "end": v(865.43, 306.4) * mm});
            skLineSegment(sketch, "E540.2", {"start": v(878.66, 293.16) * mm, "end": v(864.9, 279.4) * mm});
            skLineSegment(sketch, "E541.0", {"start": v(851.68, 266.17) * mm, "end": v(837.93, 252.42) * mm});
            skLineSegment(sketch, "E541.1", {"start": v(837.93, 252.42) * mm, "end": v(824.7, 265.66) * mm});
            skLineSegment(sketch, "E541.2", {"start": v(838.44, 279.4) * mm, "end": v(824.7, 265.66) * mm});
            skLineSegment(sketch, "E542.trimOffspring", {"start": v(851.67, 266.16) * mm, "end": v(864.6, 253.23) * mm});
            skLineSegment(sketch, "E543.trimOffspring", {"start": v(851.67, 292.64) * mm, "end": v(837.1, 307.2) * mm});
            skLineSegment(sketch, "E544.0", {"start": v(1066.02, 539.02) * mm, "end": v(1002.18, 518.28) * mm});
            skLineSegment(sketch, "E544.1", {"start": v(1071.8, 521.22) * mm, "end": v(1066.02, 539.02) * mm});
            skLineSegment(sketch, "E544.2", {"start": v(1007.96, 500.47) * mm, "end": v(1071.8, 521.22) * mm});
            skLineSegment(sketch, "E544.3", {"start": v(1002.18, 518.28) * mm, "end": v(1007.96, 500.47) * mm});
            skLineSegment(sketch, "E545.0", {"start": v(1075.02, 515.98) * mm, "end": v(1027.55, 468.52) * mm});
            skLineSegment(sketch, "E545.1", {"start": v(1088.25, 502.75) * mm, "end": v(1075.02, 515.98) * mm});
            skLineSegment(sketch, "E545.2", {"start": v(1040.79, 455.28) * mm, "end": v(1088.25, 502.75) * mm});
            skLineSegment(sketch, "E545.3", {"start": v(1027.55, 468.52) * mm, "end": v(1040.79, 455.28) * mm});
            skLineSegment(sketch, "E546.0", {"start": v(1026.73, 91.1) * mm, "end": v(1074.2, 43.64) * mm});
            skLineSegment(sketch, "E546.1", {"start": v(1039.97, 104.34) * mm, "end": v(1026.73, 91.1) * mm});
            skLineSegment(sketch, "E546.2", {"start": v(1087.43, 56.88) * mm, "end": v(1039.97, 104.34) * mm});
            skLineSegment(sketch, "E546.3", {"start": v(1074.2, 43.64) * mm, "end": v(1087.43, 56.88) * mm});
            skLineSegment(sketch, "E547.0", {"start": v(1071.8, 37.58) * mm, "end": v(1007.96, 58.33) * mm});
            skLineSegment(sketch, "E547.1", {"start": v(1066.02, 19.78) * mm, "end": v(1071.8, 37.58) * mm});
            skLineSegment(sketch, "E547.2", {"start": v(1002.18, 40.52) * mm, "end": v(1066.02, 19.78) * mm});
            skLineSegment(sketch, "E547.3", {"start": v(1007.96, 58.33) * mm, "end": v(1002.18, 40.52) * mm});
            skLineSegment(sketch, "E548.0", {"start": v(534.7, 279.4) * mm, "end": v(558.8, 353.55) * mm});
            skLineSegment(sketch, "E549.0", {"start": v(558.8, 353.55) * mm, "end": v(582.9, 279.4) * mm});
            skLineSegment(sketch, "E550.0", {"start": v(558.8, 205.25) * mm, "end": v(534.7, 279.4) * mm});
            skLineSegment(sketch, "E551.0", {"start": v(582.9, 279.4) * mm, "end": v(558.8, 205.25) * mm});
            skLineSegment(sketch, "E552.0", {"start": v(301.62, 256.95) * mm, "end": v(414.37, 369.7) * mm});
            skLineSegment(sketch, "E553.0", {"start": v(315.37, 288.1) * mm, "end": v(324.07, 279.4) * mm});
            skLineSegment(sketch, "E554", {"start": v(324.07, 279.4) * mm, "end": v(417.33, 186.14) * mm});
            skLineSegment(sketch, "E555.0", {"start": v(324.07, 234.5) * mm, "end": v(346.52, 256.95) * mm});
            skLineSegment(sketch, "E556.0", {"start": v(368.97, 279.4) * mm, "end": v(413.05, 235.32) * mm});
            skLineSegment(sketch, "E557.0", {"start": v(377.87, 333.2) * mm, "end": v(487.23, 297.67) * mm});
            skLineSegment(sketch, "E558.0", {"start": v(487.23, 261.13) * mm, "end": v(377.87, 225.6) * mm});
            skLineSegment(sketch, "E559", {"start": v(368.97, 279.4) * mm, "end": v(413.05, 323.48) * mm});
            skLineSegment(sketch, "E560.0", {"start": v(793.53, 279.4) * mm, "end": v(739.73, 225.6) * mm});
            skLineSegment(sketch, "E561", {"start": v(793.53, 279.4) * mm, "end": v(739.73, 333.2) * mm});
            skLineSegment(sketch, "E562.0", {"start": v(748.63, 279.4) * mm, "end": v(705.84, 322.19) * mm});
            skLineSegment(sketch, "E563.0", {"start": v(705.84, 322.19) * mm, "end": v(739.73, 333.2) * mm});
            skLineSegment(sketch, "E564.0", {"start": v(739.73, 225.6) * mm, "end": v(705.84, 236.61) * mm});
            skLineSegment(sketch, "E565.trimOffspring", {"start": v(748.63, 279.4) * mm, "end": v(705.84, 236.61) * mm});
            skLineSegment(sketch, "E566.0", {"start": v(681.61, 507.6) * mm, "end": v(573.57, 472.49) * mm});
            skLineSegment(sketch, "E567.0", {"start": v(544.03, 472.49) * mm, "end": v(435.99, 507.6) * mm});
            skLineSegment(sketch, "E568", {"start": v(573.57, 472.49) * mm, "end": v(544.03, 472.49) * mm});
            skLineSegment(sketch, "E569.0", {"start": v(656.42, 532.8) * mm, "end": v(563.76, 502.69) * mm});
            skLineSegment(sketch, "E570.0", {"start": v(553.84, 502.69) * mm, "end": v(461.18, 532.8) * mm});
            skLineSegment(sketch, "E571.0", {"start": v(573.57, 504.24) * mm, "end": v(544.03, 504.24) * mm});
            skLineSegment(sketch, "E572.0", {"start": v(1109.87, 79.33) * mm, "end": v(645.6, 543.61) * mm, "construction": true});
            skLineSegment(sketch, "E573", {"start": v(681.61, 507.6) * mm, "end": v(656.42, 532.8) * mm});
            skLineSegment(sketch, "E574.0", {"start": v(6.9, 78.5) * mm, "end": v(472, 543.61) * mm, "construction": true});
            skLineSegment(sketch, "E575", {"start": v(435.99, 507.6) * mm, "end": v(461.18, 532.8) * mm});
            skLineSegment(sketch, "E576.0", {"start": v(573.57, 86.31) * mm, "end": v(681.61, 51.2) * mm});
            skLineSegment(sketch, "E577.0", {"start": v(435.99, 51.2) * mm, "end": v(544.03, 86.31) * mm});
            skLineSegment(sketch, "E578", {"start": v(573.57, 86.31) * mm, "end": v(544.03, 86.31) * mm});
            skLineSegment(sketch, "E579.0", {"start": v(568.54, 54.56) * mm, "end": v(656.41, 26) * mm});
            skLineSegment(sketch, "E579.1", {"start": v(568.54, 54.56) * mm, "end": v(549.06, 54.56) * mm});
            skLineSegment(sketch, "E579.2", {"start": v(461.18, 26) * mm, "end": v(549.06, 54.56) * mm});
            skLineSegment(sketch, "E580.0", {"start": v(645.48, 15.08) * mm, "end": v(1110.7, 480.3) * mm, "construction": true});
            skLineSegment(sketch, "E581.0", {"start": v(6.9, 480.29) * mm, "end": v(472.11, 15.08) * mm, "construction": true});
            skLineSegment(sketch, "E582", {"start": v(656.41, 26) * mm, "end": v(681.61, 51.2) * mm});
            skLineSegment(sketch, "E583", {"start": v(461.18, 26) * mm, "end": v(435.99, 51.2) * mm});
            skPoint(sketch, "E584.endSnap0", {"position": v(943.51, 279.35) * mm});
            skLineSegment(sketch, "E585.0", {"start": v(909.8, 279.4) * mm, "end": v(887.36, 301.85) * mm});
            skLineSegment(sketch, "E586.0", {"start": v(909.8, 279.4) * mm, "end": v(887.36, 256.95) * mm});
            skLineSegment(sketch, "E587", {"start": v(909.8, 279.4) * mm, "end": v(1012.22, 381.81) * mm});
            skLineSegment(sketch, "E588", {"start": v(909.8, 279.4) * mm, "end": v(987.78, 201.43) * mm});
            skLineSegment(sketch, "E589.0", {"start": v(927.77, 306.34) * mm, "end": v(932.26, 301.85) * mm});
            skLineSegment(sketch, "E590.trimOffspring", {"start": v(954.7, 279.4) * mm, "end": v(1028.36, 205.75) * mm});
            skLineSegment(sketch, "E591.0", {"start": v(927.77, 252.46) * mm, "end": v(932.26, 256.95) * mm});
            skLineSegment(sketch, "E592.trimOffspring", {"start": v(954.7, 279.4) * mm, "end": v(1040.28, 364.98) * mm});
            skPoint(sketch, "E593", {"position": v(997.5, 322.19) * mm});
            skPoint(sketch, "E594", {"position": v(997.5, 236.61) * mm});
            skLineSegment(sketch, "E595", {"start": v(997.5, 236.61) * mm, "end": v(963.6, 225.6) * mm});
            skLineSegment(sketch, "E596", {"start": v(997.5, 322.19) * mm, "end": v(963.6, 333.2) * mm});
            skLineSegment(sketch, "E597.0", {"start": v(154, 333.2) * mm, "end": v(230.24, 256.95) * mm});
            skLineSegment(sketch, "E598.0", {"start": v(154, 225.6) * mm, "end": v(230.24, 301.85) * mm});
            skLineSegment(sketch, "E599.0", {"start": v(120.1, 322.19) * mm, "end": v(162.9, 279.4) * mm});
            skLineSegment(sketch, "E600.0", {"start": v(120.1, 236.61) * mm, "end": v(162.9, 279.4) * mm});
            skPoint(sketch, "E601", {"position": v(120.1, 236.61) * mm});
            skPoint(sketch, "E602", {"position": v(120.1, 322.19) * mm});
            skLineSegment(sketch, "E603", {"start": v(120.1, 236.61) * mm, "end": v(154, 225.6) * mm});
            skLineSegment(sketch, "E604", {"start": v(120.1, 322.19) * mm, "end": v(154, 333.2) * mm});
            skLineSegment(sketch, "E605.0", {"start": v(1100.61, 535.29) * mm, "end": v(1091.94, 562) * mm});
            skLineSegment(sketch, "E606.0", {"start": v(1116.28, 519.62) * mm, "end": v(1100.61, 535.29) * mm});
            skLineSegment(sketch, "E607.0", {"start": v(25.66, 562) * mm, "end": v(16.82, 534.79) * mm});
            skLineSegment(sketch, "E608.0", {"start": v(16.82, 534.79) * mm, "end": v(1.32, 519.28) * mm});
            skLineSegment(sketch, "E609.0", {"start": v(16.98, 23.53) * mm, "end": v(25.66, -3.2) * mm});
            skLineSegment(sketch, "E610.0", {"start": v(16.98, 23.53) * mm, "end": v(1.32, 39.19) * mm});
            skLineSegment(sketch, "E611.0", {"start": v(1091.94, -3.2) * mm, "end": v(1101.4, 25.95) * mm});
            skLineSegment(sketch, "E612.0", {"start": v(1101.4, 25.95) * mm, "end": v(1116.28, 40.83) * mm});
            skLineSegment(sketch, "E613", {"start": v(51.58, 19.78) * mm, "end": v(51.58, -11.97) * mm, "construction": true});
            skLineSegment(sketch, "E614", {"start": v(29.35, 56.06) * mm, "end": v(-2.4, 56.06) * mm, "construction": true});
            skLineSegment(sketch, "E615", {"start": v(-2.4, 48.17) * mm, "end": v(-2.4, 510.3) * mm});
            skLineSegment(sketch, "E616", {"start": v(1120, 510.64) * mm, "end": v(1120, 49.8) * mm});
            skLineSegment(sketch, "E617", {"start": v(1079.86, 570.77) * mm, "end": v(37.74, 570.77) * mm});
            skPoint(sketch, "E618.orphan", {"position": v(1134.92, -0.05) * mm});
            skLineSegment(sketch, "E619", {"start": v(1079.86, -11.97) * mm, "end": v(37.74, -11.97) * mm});
            skPoint(sketch, "E620.visualSharp", {"position": v(28.51, 570.77) * mm});
            skArc(sketch, "E620.filletArc", {"start": v(37.74, 570.77) * mm, "mid": v(30.28, 568.35) * mm, "end": v(25.66, 562) * mm});
            skPoint(sketch, "E621.visualSharp", {"position": v(-2.4, 515.56) * mm});
            skArc(sketch, "E621.filletArc", {"start": v(1.32, 519.28) * mm, "mid": v(-1.43, 515.16) * mm, "end": v(-2.4, 510.3) * mm});
            skPoint(sketch, "E622.visualSharp", {"position": v(-2.4, 42.9) * mm});
            skArc(sketch, "E622.filletArc", {"start": v(-2.4, 48.17) * mm, "mid": v(-1.43, 43.3) * mm, "end": v(1.32, 39.19) * mm});
            skPoint(sketch, "E623.visualSharp", {"position": v(28.51, -11.97) * mm});
            skArc(sketch, "E623.filletArc", {"start": v(25.66, -3.2) * mm, "mid": v(30.28, -9.55) * mm, "end": v(37.74, -11.97) * mm});
            skPoint(sketch, "E624.visualSharp", {"position": v(1120, 44.55) * mm});
            skArc(sketch, "E624.filletArc", {"start": v(1116.28, 40.83) * mm, "mid": v(1119.04, 44.95) * mm, "end": v(1120, 49.8) * mm});
            skPoint(sketch, "E625.visualSharp", {"position": v(1089.09, -11.97) * mm});
            skArc(sketch, "E625.filletArc", {"start": v(1079.86, -11.97) * mm, "mid": v(1087.32, -9.54) * mm, "end": v(1091.94, -3.2) * mm});
            skPoint(sketch, "E626.visualSharp", {"position": v(1089.09, 570.77) * mm});
            skArc(sketch, "E626.filletArc", {"start": v(1091.94, 562) * mm, "mid": v(1087.32, 568.35) * mm, "end": v(1079.86, 570.77) * mm});
            skPoint(sketch, "E627.visualSharp", {"position": v(1120, 515.9) * mm});
            skArc(sketch, "E627.filletArc", {"start": v(1120, 510.64) * mm, "mid": v(1119.04, 515.5) * mm, "end": v(1116.28, 519.62) * mm});
            skSolve(sketch);
        }
        {
            var Q0;
            Q0=makeQuery(id+"F27.imprint","IMPRINT",FACE,{"disambiguationData":[TD([[makeQuery(id+"F27.imprint","IMPRINT",EDGE,{"derivedFrom":sQuery(id+"F27.wireOp",EDGE,"E526.0")}),-1.0]])]});
            extrude(context, id + "F28", {"entities" : qUnion([Q0]), "depth" : 18.26 * mm});
        }
        {
            var Q0;
            Q0=qCreatedBy(makeId("Top.planeOp"),FACE);
            var sketch = newSketch(context, id + "F29", { "sketchPlane" : qUnion([Q0])});
            skLineSegment(sketch, "E628.0", {"start": v(28.32, 30.47) * mm, "end": v(31.6, 20.36) * mm});
            skLineSegment(sketch, "E629.0", {"start": v(28.32, 30.47) * mm, "end": v(21.29, 37.5) * mm});
            skLineSegment(sketch, "E630.0", {"start": v(64.76, 3.86) * mm, "end": v(86.95, 11.07) * mm});
            skLineSegment(sketch, "E631.0", {"start": v(21.29, 75.16) * mm, "end": v(37.65, 91.52) * mm});
            skLineSegment(sketch, "E632", {"start": v(17.57, 46.48) * mm, "end": v(17.57, 66.18) * mm});
            skLineSegment(sketch, "E633", {"start": v(38.12, 12.87) * mm, "end": v(55.27, 4.52) * mm});
            skLineSegment(sketch, "E634", {"start": v(28.32, 30.47) * mm, "end": v(139.2, 98.42) * mm, "construction": true});
            skLineSegment(sketch, "E635", {"start": v(94.14, 17) * mm, "end": v(128.35, 78.81) * mm});
            skLineSegment(sketch, "E636", {"start": v(46.2, 95.23) * mm, "end": v(116.8, 97.66) * mm});
            skPoint(sketch, "E637.visualSharp", {"position": v(17.57, 71.44) * mm});
            skArc(sketch, "E637.filletArc", {"start": v(21.29, 75.16) * mm, "mid": v(18.53, 71.04) * mm, "end": v(17.57, 66.18) * mm});
            skPoint(sketch, "E638.visualSharp", {"position": v(17.57, 41.22) * mm});
            skArc(sketch, "E638.filletArc", {"start": v(17.57, 46.48) * mm, "mid": v(18.53, 41.62) * mm, "end": v(21.29, 37.5) * mm});
            skPoint(sketch, "E639.visualSharp", {"position": v(33.27, 15.23) * mm});
            skArc(sketch, "E639.filletArc", {"start": v(31.6, 20.36) * mm, "mid": v(34.1, 15.95) * mm, "end": v(38.12, 12.87) * mm});
            skPoint(sketch, "E640.visualSharp", {"position": v(59.88, 2.27) * mm});
            skArc(sketch, "E640.filletArc", {"start": v(55.27, 4.52) * mm, "mid": v(59.95, 3.27) * mm, "end": v(64.76, 3.86) * mm});
            skPoint(sketch, "E641.visualSharp", {"position": v(91.72, 12.62) * mm});
            skArc(sketch, "E641.filletArc", {"start": v(86.95, 11.07) * mm, "mid": v(91.11, 13.35) * mm, "end": v(94.14, 17) * mm});
            skPoint(sketch, "E642.visualSharp", {"position": v(41.19, 95.06) * mm});
            skArc(sketch, "E642.filletArc", {"start": v(46.2, 95.23) * mm, "mid": v(41.57, 94.19) * mm, "end": v(37.65, 91.52) * mm});
            skPoint(sketch, "E643.visualSharp", {"position": v(139.2, 98.42) * mm});
            skArc(sketch, "E643.filletArc", {"start": v(128.35, 78.81) * mm, "mid": v(128.07, 91.6) * mm, "end": v(116.8, 97.66) * mm});
            skLineSegment(sketch, "E644.0", {"start": v(29.35, 56.06) * mm, "end": v(56.62, 83.32) * mm});
            skLineSegment(sketch, "E645.0", {"start": v(42.59, 42.82) * mm, "end": v(29.35, 56.06) * mm});
            skLineSegment(sketch, "E646.0", {"start": v(42.59, 42.82) * mm, "end": v(69.85, 70.09) * mm});
            skLineSegment(sketch, "E647.0", {"start": v(69.85, 70.09) * mm, "end": v(56.62, 83.32) * mm});
            skLineSegment(sketch, "E648.0", {"start": v(45.8, 37.58) * mm, "end": v(82.48, 49.5) * mm});
            skLineSegment(sketch, "E649.0", {"start": v(82.48, 49.5) * mm, "end": v(88.26, 31.7) * mm});
            skLineSegment(sketch, "E650.0", {"start": v(51.58, 19.78) * mm, "end": v(88.26, 31.7) * mm});
            skLineSegment(sketch, "E651.0", {"start": v(45.8, 37.58) * mm, "end": v(51.58, 19.78) * mm});
            skSolve(sketch);
        }
        {
            var Q0;
            Q0 = qSketchRegion(id + "F29", true);
            extrude(context, id + "F30", {"entities" : qUnion([Q0]), "depth" : 18.26 * mm});
        }
    });
